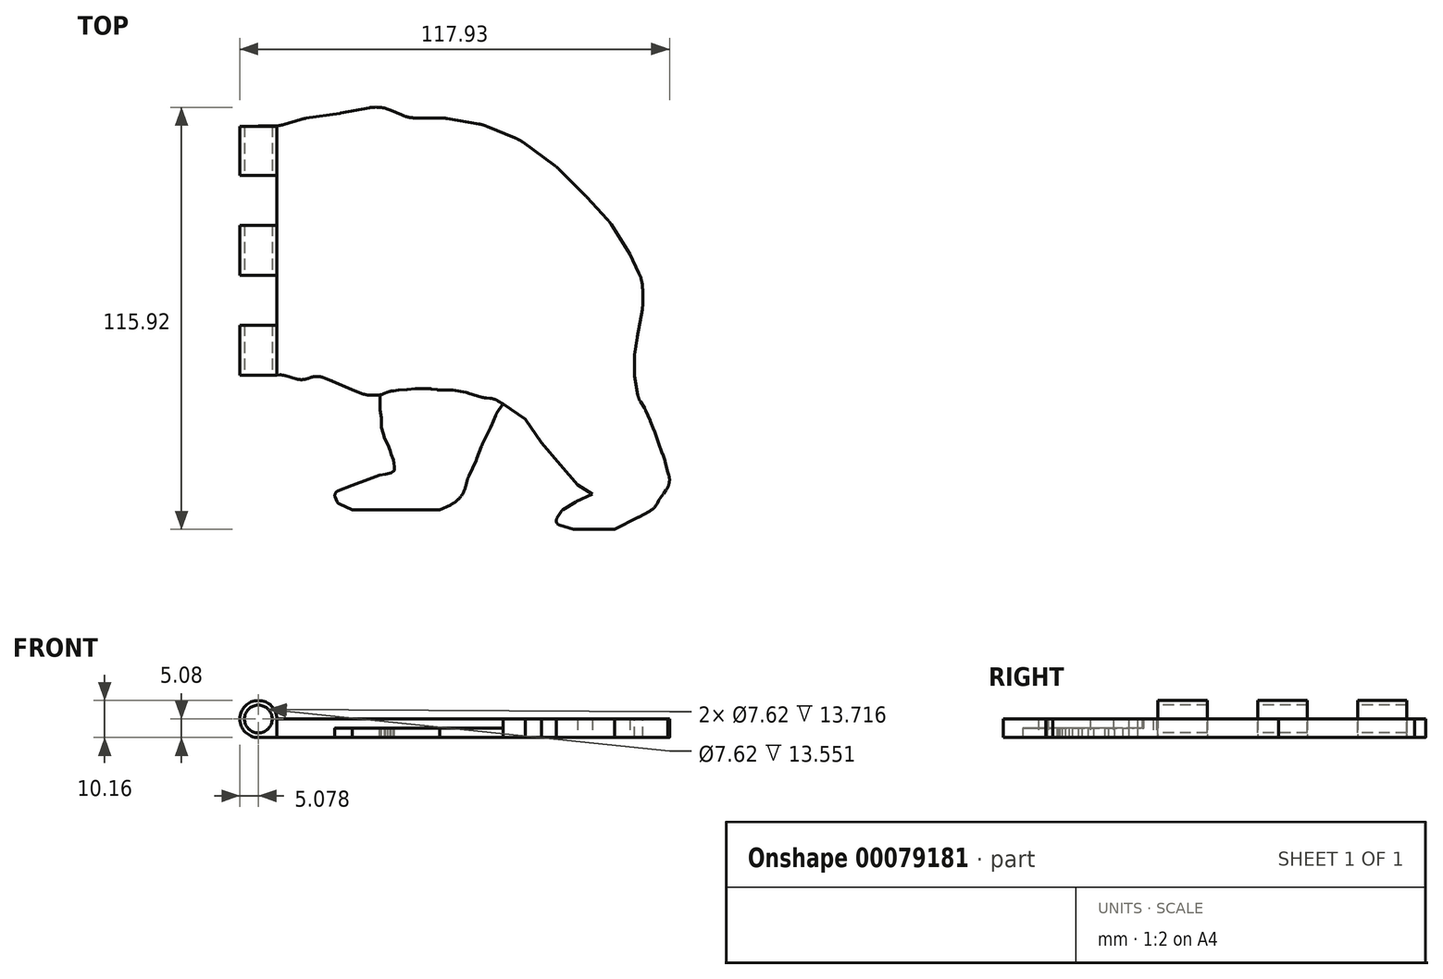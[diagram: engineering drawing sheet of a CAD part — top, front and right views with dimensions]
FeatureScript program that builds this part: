
annotation { "Feature Type Name" : "Feature", "Feature Type Description" : "" }
export const myFeature = defineFeature(function(context is Context, id is Id, definition is map)
    precondition{}
    {
        {
            var Q0;
            Q0=qCreatedBy(makeId("Top.planeOp"),FACE);
            var sketch = newSketch(context, id + "F0", { "sketchPlane" : qUnion([Q0])});
            skLineSegment(sketch, "E0", {"start": v(-108.98, 47.54) * mm, "end": v(-114.56, 51.08) * mm});
            skLineSegment(sketch, "E1", {"start": v(-114.56, 51.08) * mm, "end": v(-115.99, 48.82) * mm});
            skLineSegment(sketch, "E2", {"start": v(-115.99, 48.82) * mm, "end": v(-117.54, 46.98) * mm});
            skLineSegment(sketch, "E3", {"start": v(-117.54, 46.98) * mm, "end": v(-115.49, 40.84) * mm});
            skLineSegment(sketch, "E4", {"start": v(-115.49, 40.84) * mm, "end": v(-119.38, 33.2) * mm});
            skLineSegment(sketch, "E5", {"start": v(-119.38, 33.2) * mm, "end": v(-119.38, 25.58) * mm});
            skLineSegment(sketch, "E6", {"start": v(-119.38, 25.58) * mm, "end": v(-119.38, 18.5) * mm});
            skLineSegment(sketch, "E7", {"start": v(-119.38, 18.5) * mm, "end": v(-122.93, 10.13) * mm});
            skLineSegment(sketch, "E8", {"start": v(-122.93, 10.13) * mm, "end": v(-125.17, 4.36) * mm});
            skLineSegment(sketch, "E9", {"start": v(-125.17, 4.36) * mm, "end": v(-125.17, 0) * mm});
            skLineSegment(sketch, "E10", {"start": v(-125.17, 0) * mm, "end": v(-117.16, -4.2) * mm});
            skLineSegment(sketch, "E11", {"start": v(-117.16, -4.2) * mm, "end": v(-112.7, -1.4) * mm});
            skLineSegment(sketch, "E12", {"start": v(-112.7, -1.4) * mm, "end": v(-103.77, 3.25) * mm});
            skLineSegment(sketch, "E13", {"start": v(-103.77, 3.25) * mm, "end": v(-97.07, 5.48) * mm});
            skLineSegment(sketch, "E14", {"start": v(-97.07, 5.48) * mm, "end": v(-88.5, 7.16) * mm});
            skLineSegment(sketch, "E15", {"start": v(-88.5, 7.16) * mm, "end": v(-93.16, 2.13) * mm});
            skLineSegment(sketch, "E16", {"start": v(-93.16, 2.13) * mm, "end": v(-99.49, -4.94) * mm});
            skLineSegment(sketch, "E17", {"start": v(-99.49, -4.94) * mm, "end": v(-104.32, -11.08) * mm});
            skLineSegment(sketch, "E18", {"start": v(-104.32, -11.08) * mm, "end": v(-106, -14.62) * mm});
            skLineSegment(sketch, "E19", {"start": v(-106, -14.62) * mm, "end": v(-107.86, -19.08) * mm});
            skLineSegment(sketch, "E20", {"start": v(-107.86, -19.08) * mm, "end": v(-110.1, -25.23) * mm});
            skLineSegment(sketch, "E21", {"start": v(-110.1, -25.23) * mm, "end": v(-110.1, -28.95) * mm});
            skLineSegment(sketch, "E22", {"start": v(-110.1, -28.95) * mm, "end": v(-111.77, -33.04) * mm});
            skLineSegment(sketch, "E23", {"start": v(-111.77, -33.04) * mm, "end": v(-109.14, -34.12) * mm});
            skLineSegment(sketch, "E24", {"start": v(-109.14, -34.12) * mm, "end": v(-103.2, -30.8) * mm});
            skLineSegment(sketch, "E25", {"start": v(-103.2, -30.8) * mm, "end": v(-100.6, -27.64) * mm});
            skLineSegment(sketch, "E26", {"start": v(-100.6, -27.64) * mm, "end": v(-97.07, -19.27) * mm});
            skLineSegment(sketch, "E27", {"start": v(-97.07, -19.27) * mm, "end": v(-92.23, -17.4) * mm});
            skLineSegment(sketch, "E28", {"start": v(-92.23, -17.4) * mm, "end": v(-75.66, -17.4) * mm});
            skLineSegment(sketch, "E29", {"start": v(-75.66, -17.4) * mm, "end": v(-63, -11.45) * mm});
            skLineSegment(sketch, "E30", {"start": v(-63, -11.45) * mm, "end": v(-65.24, -20.39) * mm});
            skLineSegment(sketch, "E31", {"start": v(-65.24, -20.39) * mm, "end": v(-67.3, -29.13) * mm});
            skLineSegment(sketch, "E32", {"start": v(-67.3, -29.13) * mm, "end": v(-70.64, -34.9) * mm});
            skLineSegment(sketch, "E33", {"start": v(-70.64, -34.9) * mm, "end": v(-73.06, -36.76) * mm});
            skLineSegment(sketch, "E34", {"start": v(-73.06, -36.76) * mm, "end": v(-80.5, -36.76) * mm});
            skLineSegment(sketch, "E35", {"start": v(-80.5, -36.76) * mm, "end": v(-84.78, -38.62) * mm});
            skLineSegment(sketch, "E36", {"start": v(-84.78, -38.62) * mm, "end": v(-87.95, -42.35) * mm});
            skLineSegment(sketch, "E37", {"start": v(-87.95, -42.35) * mm, "end": v(-90, -44.95) * mm});
            skLineSegment(sketch, "E38", {"start": v(-90, -44.95) * mm, "end": v(-87.38, -47) * mm});
            skLineSegment(sketch, "E39", {"start": v(-87.38, -47) * mm, "end": v(-77.71, -47) * mm});
            skLineSegment(sketch, "E40", {"start": v(-77.71, -47) * mm, "end": v(-69.9, -47) * mm});
            skLineSegment(sketch, "E41", {"start": v(-69.9, -47) * mm, "end": v(-63.38, -45.32) * mm});
            skLineSegment(sketch, "E42", {"start": v(-63.38, -45.32) * mm, "end": v(-55.57, -41.79) * mm});
            skLineSegment(sketch, "E43", {"start": v(-55.57, -41.79) * mm, "end": v(-47.94, -37.7) * mm});
            skLineSegment(sketch, "E44", {"start": v(-47.94, -37.7) * mm, "end": v(-42.73, -32.67) * mm});
            skLineSegment(sketch, "E45", {"start": v(-42.73, -32.67) * mm, "end": v(-40.12, -28.76) * mm});
            skLineSegment(sketch, "E46", {"start": v(-40.12, -28.76) * mm, "end": v(-36.96, -22.62) * mm});
            skLineSegment(sketch, "E47", {"start": v(-36.96, -22.62) * mm, "end": v(-33.8, -16.48) * mm});
            skLineSegment(sketch, "E48", {"start": v(-33.8, -16.48) * mm, "end": v(-29.14, -10.9) * mm});
            skLineSegment(sketch, "E49", {"start": v(-29.14, -10.9) * mm, "end": v(-23.56, -9.03) * mm});
            skLineSegment(sketch, "E50", {"start": v(-23.56, -9.03) * mm, "end": v(-19.1, -8.85) * mm});
            skLineSegment(sketch, "E51", {"start": v(-19.1, -8.85) * mm, "end": v(-13.5, -10.52) * mm});
            skLineSegment(sketch, "E52", {"start": v(-13.5, -10.52) * mm, "end": v(-9.97, -8.85) * mm});
            skLineSegment(sketch, "E53", {"start": v(-9.97, -8.85) * mm, "end": v(-5.5, -10.52) * mm});
            skLineSegment(sketch, "E54", {"start": v(-5.5, -10.52) * mm, "end": v(0, -12.94) * mm});
            skLineSegment(sketch, "E55", {"start": v(0, -12.94) * mm, "end": v(3.99, -14.43) * mm});
            skLineSegment(sketch, "E56", {"start": v(3.99, -14.43) * mm, "end": v(7.7, -14.43) * mm});
            skLineSegment(sketch, "E57", {"start": v(7.7, -14.43) * mm, "end": v(7.7, -18.53) * mm});
            skLineSegment(sketch, "E58", {"start": v(7.7, -18.53) * mm, "end": v(5.29, -22.43) * mm});
            skLineSegment(sketch, "E59", {"start": v(5.29, -22.43) * mm, "end": v(6.22, -25.23) * mm});
            skLineSegment(sketch, "E60", {"start": v(6.22, -25.23) * mm, "end": v(6.96, -29.88) * mm});
            skLineSegment(sketch, "E61", {"start": v(6.96, -29.88) * mm, "end": v(8.45, -33.23) * mm});
            skLineSegment(sketch, "E62", {"start": v(8.45, -33.23) * mm, "end": v(10.5, -35.27) * mm});
            skLineSegment(sketch, "E63", {"start": v(10.5, -35.27) * mm, "end": v(4.54, -37.5) * mm});
            skLineSegment(sketch, "E64", {"start": v(4.54, -37.5) * mm, "end": v(0, -39.18) * mm});
            skLineSegment(sketch, "E65", {"start": v(0, -39.18) * mm, "end": v(-5.13, -41.23) * mm});
            skLineSegment(sketch, "E66", {"start": v(-5.13, -41.23) * mm, "end": v(-4, -44.09) * mm});
            skLineSegment(sketch, "E67", {"start": v(-4, -44.09) * mm, "end": v(0, -45.88) * mm});
            skLineSegment(sketch, "E68", {"start": v(0, -45.88) * mm, "end": v(6.22, -45.88) * mm});
            skLineSegment(sketch, "E69", {"start": v(6.22, -45.88) * mm, "end": v(16.08, -45.88) * mm});
            skLineSegment(sketch, "E70", {"start": v(16.08, -45.88) * mm, "end": v(24.08, -45.88) * mm});
            skLineSegment(sketch, "E71", {"start": v(24.08, -45.88) * mm, "end": v(28.18, -44.02) * mm});
            skLineSegment(sketch, "E72", {"start": v(28.18, -44.02) * mm, "end": v(30.6, -41.6) * mm});
            skLineSegment(sketch, "E73", {"start": v(30.6, -41.6) * mm, "end": v(31.71, -37.32) * mm});
            skLineSegment(sketch, "E74", {"start": v(31.71, -37.32) * mm, "end": v(34.13, -32.11) * mm});
            skLineSegment(sketch, "E75", {"start": v(34.13, -32.11) * mm, "end": v(35.62, -28.2) * mm});
            skLineSegment(sketch, "E76", {"start": v(35.62, -28.2) * mm, "end": v(38.04, -23.18) * mm});
            skLineSegment(sketch, "E77", {"start": v(38.04, -23.18) * mm, "end": v(39.72, -19.27) * mm});
            skLineSegment(sketch, "E78", {"start": v(39.72, -19.27) * mm, "end": v(41.4, -16.85) * mm});
            skLineSegment(sketch, "E79", {"start": v(41.4, -16.85) * mm, "end": v(47.47, -21.06) * mm});
            skLineSegment(sketch, "E80", {"start": v(47.47, -21.06) * mm, "end": v(52, -27.46) * mm});
            skLineSegment(sketch, "E81", {"start": v(52, -27.46) * mm, "end": v(57.2, -33.6) * mm});
            skLineSegment(sketch, "E82", {"start": v(57.2, -33.6) * mm, "end": v(61.86, -39) * mm});
            skLineSegment(sketch, "E83", {"start": v(61.86, -39) * mm, "end": v(65.96, -41.6) * mm});
            skLineSegment(sketch, "E84", {"start": v(65.96, -41.6) * mm, "end": v(61.49, -43.65) * mm});
            skLineSegment(sketch, "E85", {"start": v(61.49, -43.65) * mm, "end": v(57.58, -46.07) * mm});
            skLineSegment(sketch, "E86", {"start": v(57.58, -46.07) * mm, "end": v(55.35, -49.68) * mm});
            skLineSegment(sketch, "E87", {"start": v(55.35, -49.68) * mm, "end": v(57.58, -46.07) * mm});
            skLineSegment(sketch, "E88", {"start": v(55.35, -49.68) * mm, "end": v(60.93, -51.28) * mm});
            skLineSegment(sketch, "E89", {"start": v(60.93, -51.28) * mm, "end": v(68, -51.28) * mm});
            skLineSegment(sketch, "E90", {"start": v(68, -51.28) * mm, "end": v(72.1, -51.28) * mm});
            skLineSegment(sketch, "E91", {"start": v(72.1, -51.28) * mm, "end": v(78.61, -47.93) * mm});
            skLineSegment(sketch, "E92", {"start": v(78.61, -47.93) * mm, "end": v(83.08, -45.5) * mm});
            skLineSegment(sketch, "E93", {"start": v(83.08, -45.5) * mm, "end": v(87.17, -40.49) * mm});
            skLineSegment(sketch, "E94", {"start": v(87.17, -40.49) * mm, "end": v(89.03, -35.09) * mm});
            skLineSegment(sketch, "E95", {"start": v(89.03, -35.09) * mm, "end": v(86.24, -28.95) * mm});
            skLineSegment(sketch, "E96", {"start": v(86.24, -28.95) * mm, "end": v(84.38, -22.06) * mm});
            skLineSegment(sketch, "E97", {"start": v(84.38, -22.06) * mm, "end": v(81.22, -16.85) * mm});
            skLineSegment(sketch, "E98", {"start": v(81.22, -16.85) * mm, "end": v(79.73, -14.25) * mm});
            skLineSegment(sketch, "E99", {"start": v(79.73, -14.25) * mm, "end": v(79.73, -6.99) * mm});
            skLineSegment(sketch, "E100", {"start": v(79.73, -6.99) * mm, "end": v(79.73, 1.76) * mm});
            skLineSegment(sketch, "E101", {"start": v(79.73, 1.76) * mm, "end": v(79.73, 8.64) * mm});
            skLineSegment(sketch, "E102", {"start": v(79.73, 8.64) * mm, "end": v(79.73, 17.02) * mm});
            skLineSegment(sketch, "E103", {"start": v(79.73, 17.02) * mm, "end": v(76.2, 24.28) * mm});
            skLineSegment(sketch, "E104", {"start": v(76.2, 24.28) * mm, "end": v(70.6, 33.2) * mm});
            skLineSegment(sketch, "E105", {"start": v(70.6, 33.2) * mm, "end": v(64.28, 40.1) * mm});
            skLineSegment(sketch, "E106", {"start": v(64.28, 40.1) * mm, "end": v(56.28, 48.1) * mm});
            skLineSegment(sketch, "E107", {"start": v(56.28, 48.1) * mm, "end": v(45.86, 55.73) * mm});
            skLineSegment(sketch, "E108", {"start": v(45.86, 55.73) * mm, "end": v(36, 59.82) * mm});
            skLineSegment(sketch, "E109", {"start": v(36, 59.82) * mm, "end": v(25.2, 61.68) * mm});
            skLineSegment(sketch, "E110", {"start": v(25.2, 61.68) * mm, "end": v(15.52, 61.68) * mm});
            skLineSegment(sketch, "E111", {"start": v(15.52, 61.68) * mm, "end": v(7.7, 65.03) * mm});
            skLineSegment(sketch, "E112", {"start": v(7.7, 65.03) * mm, "end": v(-3.27, 62.99) * mm});
            skLineSegment(sketch, "E113", {"start": v(-3.27, 62.99) * mm, "end": v(-13.32, 61.5) * mm});
            skLineSegment(sketch, "E114", {"start": v(-13.32, 61.5) * mm, "end": v(-20.2, 59.45) * mm});
            skLineSegment(sketch, "E115", {"start": v(-20.2, 59.45) * mm, "end": v(-26.35, 59.45) * mm});
            skLineSegment(sketch, "E116", {"start": v(-26.35, 59.45) * mm, "end": v(-32.68, 61.68) * mm});
            skLineSegment(sketch, "E117", {"start": v(-32.68, 61.68) * mm, "end": v(-42.17, 64.47) * mm});
            skLineSegment(sketch, "E118", {"start": v(-42.17, 64.47) * mm, "end": v(-50.36, 64.47) * mm});
            skLineSegment(sketch, "E119", {"start": v(-50.36, 64.47) * mm, "end": v(-59.1, 59.08) * mm});
            skLineSegment(sketch, "E120", {"start": v(-59.1, 59.08) * mm, "end": v(-66.55, 53.87) * mm});
            skLineSegment(sketch, "E121", {"start": v(-66.55, 53.87) * mm, "end": v(-76.6, 50.14) * mm});
            skLineSegment(sketch, "E122", {"start": v(-76.6, 50.14) * mm, "end": v(-85.9, 48.47) * mm});
            skLineSegment(sketch, "E123", {"start": v(-85.9, 48.47) * mm, "end": v(-95.02, 46.6) * mm});
            skLineSegment(sketch, "E124", {"start": v(-95.02, 46.6) * mm, "end": v(-101.53, 46.05) * mm});
            skLineSegment(sketch, "E125", {"start": v(-101.53, 46.05) * mm, "end": v(-108.98, 47.54) * mm});
            skSolve(sketch);
        }
        {
            var Q0;
            Q0=qSketchRegion(id+"F0",true);
            extrude(context, id + "F1", {"entities" : qUnion([Q0]), "depth" : 5.08 * mm});
        }
        {
            var Q0;
            Q0=makeQuery(id+"F1.opExtrude","SWEPT_EDGE",EDGE,{"disambiguationData":[OSD([sQuery(id+"F0.wireOp",EDGE,"E117"),sQuery(id+"F0.wireOp",EDGE,"E118")])]});
            var Q1;
            Q1=makeQuery(id+"F1.opExtrude","SWEPT_EDGE",EDGE,{"disambiguationData":[OSD([sQuery(id+"F0.wireOp",EDGE,"E118"),sQuery(id+"F0.wireOp",EDGE,"E119")])]});
            var Q2;
            Q2=makeQuery(id+"F1.opExtrude","SWEPT_EDGE",EDGE,{"disambiguationData":[OSD([sQuery(id+"F0.wireOp",EDGE,"E119"),sQuery(id+"F0.wireOp",EDGE,"E120")])]});
            var Q3;
            Q3=makeQuery(id+"F1.opExtrude","SWEPT_EDGE",EDGE,{"disambiguationData":[OSD([sQuery(id+"F0.wireOp",EDGE,"E120"),sQuery(id+"F0.wireOp",EDGE,"E121")])]});
            var Q4;
            Q4=makeQuery(id+"F1.opExtrude","SWEPT_EDGE",EDGE,{"disambiguationData":[OSD([sQuery(id+"F0.wireOp",EDGE,"E121"),sQuery(id+"F0.wireOp",EDGE,"E122")])]});
            var Q5;
            Q5=makeQuery(id+"F1.opExtrude","SWEPT_EDGE",EDGE,{"disambiguationData":[OSD([sQuery(id+"F0.wireOp",EDGE,"E116"),sQuery(id+"F0.wireOp",EDGE,"E117")])]});
            var Q6;
            Q6=makeQuery(id+"F1.opExtrude","SWEPT_EDGE",EDGE,{"disambiguationData":[OSD([sQuery(id+"F0.wireOp",EDGE,"E115"),sQuery(id+"F0.wireOp",EDGE,"E116")])]});
            var Q7;
            Q7=makeQuery(id+"F1.opExtrude","SWEPT_EDGE",EDGE,{"disambiguationData":[OSD([sQuery(id+"F0.wireOp",EDGE,"E114"),sQuery(id+"F0.wireOp",EDGE,"E115")])]});
            var Q8;
            Q8=makeQuery(id+"F1.opExtrude","SWEPT_EDGE",EDGE,{"disambiguationData":[OSD([sQuery(id+"F0.wireOp",EDGE,"E113"),sQuery(id+"F0.wireOp",EDGE,"E114")])]});
            var Q9;
            Q9=makeQuery(id+"F1.opExtrude","SWEPT_EDGE",EDGE,{"disambiguationData":[OSD([sQuery(id+"F0.wireOp",EDGE,"E112"),sQuery(id+"F0.wireOp",EDGE,"E113")])]});
            var Q10;
            Q10=makeQuery(id+"F1.opExtrude","SWEPT_EDGE",EDGE,{"disambiguationData":[OSD([sQuery(id+"F0.wireOp",EDGE,"E111"),sQuery(id+"F0.wireOp",EDGE,"E112")])]});
            var Q11;
            Q11=makeQuery(id+"F1.opExtrude","SWEPT_EDGE",EDGE,{"disambiguationData":[OSD([sQuery(id+"F0.wireOp",EDGE,"E110"),sQuery(id+"F0.wireOp",EDGE,"E111")])]});
            var Q12;
            Q12=makeQuery(id+"F1.opExtrude","SWEPT_EDGE",EDGE,{"disambiguationData":[OSD([sQuery(id+"F0.wireOp",EDGE,"E109"),sQuery(id+"F0.wireOp",EDGE,"E110")])]});
            var Q13;
            Q13=makeQuery(id+"F1.opExtrude","SWEPT_EDGE",EDGE,{"disambiguationData":[OSD([sQuery(id+"F0.wireOp",EDGE,"E107"),sQuery(id+"F0.wireOp",EDGE,"E108")])]});
            var Q14;
            Q14=makeQuery(id+"F1.opExtrude","SWEPT_EDGE",EDGE,{"disambiguationData":[OSD([sQuery(id+"F0.wireOp",EDGE,"E108"),sQuery(id+"F0.wireOp",EDGE,"E109")])]});
            var Q15;
            Q15=makeQuery(id+"F1.opExtrude","SWEPT_EDGE",EDGE,{"disambiguationData":[OSD([sQuery(id+"F0.wireOp",EDGE,"E106"),sQuery(id+"F0.wireOp",EDGE,"E107")])]});
            var Q16;
            Q16=makeQuery(id+"F1.opExtrude","SWEPT_EDGE",EDGE,{"disambiguationData":[OSD([sQuery(id+"F0.wireOp",EDGE,"E102"),sQuery(id+"F0.wireOp",EDGE,"E103")])]});
            var Q17;
            Q17=makeQuery(id+"F1.opExtrude","SWEPT_EDGE",EDGE,{"disambiguationData":[OSD([sQuery(id+"F0.wireOp",EDGE,"E104"),sQuery(id+"F0.wireOp",EDGE,"E105")])]});
            var Q18;
            Q18=makeQuery(id+"F1.opExtrude","SWEPT_EDGE",EDGE,{"disambiguationData":[OSD([sQuery(id+"F0.wireOp",EDGE,"E105"),sQuery(id+"F0.wireOp",EDGE,"E106")])]});
            fillet(context, id + "F2", {"entities" : qUnion([Q0, Q1, Q2, Q3, Q4, Q5, Q6, Q7, Q8, Q9, Q10, Q11, Q12, Q13, Q14, Q15, Q16, Q17, Q18]), "radius" : 10.16 * mm, "tangentPropagation" : true, "allowEdgeOverflow" : false});
        }
        {
            var Q0;
            Q0=makeQuery(id+"F1.opExtrude","CAP_FACE",FACE,{"disambiguationData":[OSD([sQuery(id+"F0.wireOp",EDGE,"E0"),sQuery(id+"F0.wireOp",EDGE,"E1"),sQuery(id+"F0.wireOp",EDGE,"E2"),sQuery(id+"F0.wireOp",EDGE,"E3"),sQuery(id+"F0.wireOp",EDGE,"E4"),sQuery(id+"F0.wireOp",EDGE,"E5"),sQuery(id+"F0.wireOp",EDGE,"E6"),sQuery(id+"F0.wireOp",EDGE,"E7"),sQuery(id+"F0.wireOp",EDGE,"E8"),sQuery(id+"F0.wireOp",EDGE,"E9"),sQuery(id+"F0.wireOp",EDGE,"E10"),sQuery(id+"F0.wireOp",EDGE,"E11"),sQuery(id+"F0.wireOp",EDGE,"E12"),sQuery(id+"F0.wireOp",EDGE,"E13"),sQuery(id+"F0.wireOp",EDGE,"E14"),sQuery(id+"F0.wireOp",EDGE,"E15"),sQuery(id+"F0.wireOp",EDGE,"E16"),sQuery(id+"F0.wireOp",EDGE,"E17"),sQuery(id+"F0.wireOp",EDGE,"E18"),sQuery(id+"F0.wireOp",EDGE,"E19"),sQuery(id+"F0.wireOp",EDGE,"E20"),sQuery(id+"F0.wireOp",EDGE,"E21"),sQuery(id+"F0.wireOp",EDGE,"E22"),sQuery(id+"F0.wireOp",EDGE,"E23"),sQuery(id+"F0.wireOp",EDGE,"E24"),sQuery(id+"F0.wireOp",EDGE,"E25"),sQuery(id+"F0.wireOp",EDGE,"E26"),sQuery(id+"F0.wireOp",EDGE,"E27"),sQuery(id+"F0.wireOp",EDGE,"E28"),sQuery(id+"F0.wireOp",EDGE,"E29"),sQuery(id+"F0.wireOp",EDGE,"E30"),sQuery(id+"F0.wireOp",EDGE,"E31"),sQuery(id+"F0.wireOp",EDGE,"E32"),sQuery(id+"F0.wireOp",EDGE,"E33"),sQuery(id+"F0.wireOp",EDGE,"E34"),sQuery(id+"F0.wireOp",EDGE,"E35"),sQuery(id+"F0.wireOp",EDGE,"E36"),sQuery(id+"F0.wireOp",EDGE,"E37"),sQuery(id+"F0.wireOp",EDGE,"E38"),sQuery(id+"F0.wireOp",EDGE,"E39"),sQuery(id+"F0.wireOp",EDGE,"E40"),sQuery(id+"F0.wireOp",EDGE,"E41"),sQuery(id+"F0.wireOp",EDGE,"E42"),sQuery(id+"F0.wireOp",EDGE,"E43"),sQuery(id+"F0.wireOp",EDGE,"E44"),sQuery(id+"F0.wireOp",EDGE,"E45"),sQuery(id+"F0.wireOp",EDGE,"E46"),sQuery(id+"F0.wireOp",EDGE,"E47"),sQuery(id+"F0.wireOp",EDGE,"E48"),sQuery(id+"F0.wireOp",EDGE,"E49"),sQuery(id+"F0.wireOp",EDGE,"E50"),sQuery(id+"F0.wireOp",EDGE,"E51"),sQuery(id+"F0.wireOp",EDGE,"E52"),sQuery(id+"F0.wireOp",EDGE,"E53"),sQuery(id+"F0.wireOp",EDGE,"E54"),sQuery(id+"F0.wireOp",EDGE,"E55"),sQuery(id+"F0.wireOp",EDGE,"E56"),sQuery(id+"F0.wireOp",EDGE,"E57"),sQuery(id+"F0.wireOp",EDGE,"E58"),sQuery(id+"F0.wireOp",EDGE,"E59"),sQuery(id+"F0.wireOp",EDGE,"E60"),sQuery(id+"F0.wireOp",EDGE,"E61"),sQuery(id+"F0.wireOp",EDGE,"E62"),sQuery(id+"F0.wireOp",EDGE,"E63"),sQuery(id+"F0.wireOp",EDGE,"E64"),sQuery(id+"F0.wireOp",EDGE,"E65"),sQuery(id+"F0.wireOp",EDGE,"E66"),sQuery(id+"F0.wireOp",EDGE,"E67"),sQuery(id+"F0.wireOp",EDGE,"E68"),sQuery(id+"F0.wireOp",EDGE,"E69"),sQuery(id+"F0.wireOp",EDGE,"E70"),sQuery(id+"F0.wireOp",EDGE,"E71"),sQuery(id+"F0.wireOp",EDGE,"E72"),sQuery(id+"F0.wireOp",EDGE,"E73"),sQuery(id+"F0.wireOp",EDGE,"E74"),sQuery(id+"F0.wireOp",EDGE,"E75"),sQuery(id+"F0.wireOp",EDGE,"E76"),sQuery(id+"F0.wireOp",EDGE,"E77"),sQuery(id+"F0.wireOp",EDGE,"E78"),sQuery(id+"F0.wireOp",EDGE,"E79"),sQuery(id+"F0.wireOp",EDGE,"E80"),sQuery(id+"F0.wireOp",EDGE,"E81"),sQuery(id+"F0.wireOp",EDGE,"E82"),sQuery(id+"F0.wireOp",EDGE,"E83"),sQuery(id+"F0.wireOp",EDGE,"E84"),sQuery(id+"F0.wireOp",EDGE,"E85"),sQuery(id+"F0.wireOp",EDGE,"E87"),sQuery(id+"F0.wireOp",EDGE,"E88"),sQuery(id+"F0.wireOp",EDGE,"E89"),sQuery(id+"F0.wireOp",EDGE,"E90"),sQuery(id+"F0.wireOp",EDGE,"E91"),sQuery(id+"F0.wireOp",EDGE,"E92"),sQuery(id+"F0.wireOp",EDGE,"E93"),sQuery(id+"F0.wireOp",EDGE,"E94"),sQuery(id+"F0.wireOp",EDGE,"E95"),sQuery(id+"F0.wireOp",EDGE,"E96"),sQuery(id+"F0.wireOp",EDGE,"E97"),sQuery(id+"F0.wireOp",EDGE,"E98"),sQuery(id+"F0.wireOp",EDGE,"E99"),sQuery(id+"F0.wireOp",EDGE,"E100"),sQuery(id+"F0.wireOp",EDGE,"E101"),sQuery(id+"F0.wireOp",EDGE,"E102"),sQuery(id+"F0.wireOp",EDGE,"E103"),sQuery(id+"F0.wireOp",EDGE,"E104"),sQuery(id+"F0.wireOp",EDGE,"E105"),sQuery(id+"F0.wireOp",EDGE,"E106"),sQuery(id+"F0.wireOp",EDGE,"E107"),sQuery(id+"F0.wireOp",EDGE,"E108"),sQuery(id+"F0.wireOp",EDGE,"E109"),sQuery(id+"F0.wireOp",EDGE,"E110"),sQuery(id+"F0.wireOp",EDGE,"E111"),sQuery(id+"F0.wireOp",EDGE,"E112"),sQuery(id+"F0.wireOp",EDGE,"E113"),sQuery(id+"F0.wireOp",EDGE,"E114"),sQuery(id+"F0.wireOp",EDGE,"E115"),sQuery(id+"F0.wireOp",EDGE,"E116"),sQuery(id+"F0.wireOp",EDGE,"E117"),sQuery(id+"F0.wireOp",EDGE,"E118"),sQuery(id+"F0.wireOp",EDGE,"E119"),sQuery(id+"F0.wireOp",EDGE,"E120"),sQuery(id+"F0.wireOp",EDGE,"E121"),sQuery(id+"F0.wireOp",EDGE,"E122"),sQuery(id+"F0.wireOp",EDGE,"E123"),sQuery(id+"F0.wireOp",EDGE,"E124"),sQuery(id+"F0.wireOp",EDGE,"E125")])],"isStart":false});
            var sketch = newSketch(context, id + "F3", { "sketchPlane" : qUnion([Q0])});
            skLineSegment(sketch, "E126", {"start": v(79.73, 14.68) * mm, "end": v(79.73, 9.47) * mm});
            skLineSegment(sketch, "E127", {"start": v(79.73, 9.47) * mm, "end": v(78.29, 1.47) * mm});
            skLineSegment(sketch, "E128", {"start": v(78.29, 1.47) * mm, "end": v(77.45, -3.82) * mm});
            skLineSegment(sketch, "E129", {"start": v(77.45, -3.82) * mm, "end": v(77.45, -8.77) * mm});
            skLineSegment(sketch, "E130", {"start": v(77.45, -8.77) * mm, "end": v(79.94, -14.62) * mm});
            skLineSegment(sketch, "E131", {"start": v(79.94, -14.62) * mm, "end": v(89.3, -16.02) * mm});
            skLineSegment(sketch, "E132", {"start": v(89.3, -16.02) * mm, "end": v(87.14, 16.67) * mm});
            skLineSegment(sketch, "E133", {"start": v(87.14, 16.67) * mm, "end": v(79.73, 14.68) * mm});
            skSolve(sketch);
        }
        {
            var Q0;
            Q0=qSketchRegion(id+"F3",true);
            extrude(context, id + "F4", {"entities" : qUnion([Q0]), "operationType" : NewBodyOperationType.REMOVE, "oppositeDirection" : true, "depth" : 25.4 * mm});
        }
        {
            var Q0;
            Q0=makeQuery(id+"F1.opExtrude","CAP_FACE",FACE,{"disambiguationData":[OSD([sQuery(id+"F0.wireOp",EDGE,"E0"),sQuery(id+"F0.wireOp",EDGE,"E1"),sQuery(id+"F0.wireOp",EDGE,"E2"),sQuery(id+"F0.wireOp",EDGE,"E3"),sQuery(id+"F0.wireOp",EDGE,"E4"),sQuery(id+"F0.wireOp",EDGE,"E5"),sQuery(id+"F0.wireOp",EDGE,"E6"),sQuery(id+"F0.wireOp",EDGE,"E7"),sQuery(id+"F0.wireOp",EDGE,"E8"),sQuery(id+"F0.wireOp",EDGE,"E9"),sQuery(id+"F0.wireOp",EDGE,"E10"),sQuery(id+"F0.wireOp",EDGE,"E11"),sQuery(id+"F0.wireOp",EDGE,"E12"),sQuery(id+"F0.wireOp",EDGE,"E13"),sQuery(id+"F0.wireOp",EDGE,"E14"),sQuery(id+"F0.wireOp",EDGE,"E15"),sQuery(id+"F0.wireOp",EDGE,"E16"),sQuery(id+"F0.wireOp",EDGE,"E17"),sQuery(id+"F0.wireOp",EDGE,"E18"),sQuery(id+"F0.wireOp",EDGE,"E19"),sQuery(id+"F0.wireOp",EDGE,"E20"),sQuery(id+"F0.wireOp",EDGE,"E21"),sQuery(id+"F0.wireOp",EDGE,"E22"),sQuery(id+"F0.wireOp",EDGE,"E23"),sQuery(id+"F0.wireOp",EDGE,"E24"),sQuery(id+"F0.wireOp",EDGE,"E25"),sQuery(id+"F0.wireOp",EDGE,"E26"),sQuery(id+"F0.wireOp",EDGE,"E27"),sQuery(id+"F0.wireOp",EDGE,"E28"),sQuery(id+"F0.wireOp",EDGE,"E29"),sQuery(id+"F0.wireOp",EDGE,"E30"),sQuery(id+"F0.wireOp",EDGE,"E31"),sQuery(id+"F0.wireOp",EDGE,"E32"),sQuery(id+"F0.wireOp",EDGE,"E33"),sQuery(id+"F0.wireOp",EDGE,"E34"),sQuery(id+"F0.wireOp",EDGE,"E35"),sQuery(id+"F0.wireOp",EDGE,"E36"),sQuery(id+"F0.wireOp",EDGE,"E37"),sQuery(id+"F0.wireOp",EDGE,"E38"),sQuery(id+"F0.wireOp",EDGE,"E39"),sQuery(id+"F0.wireOp",EDGE,"E40"),sQuery(id+"F0.wireOp",EDGE,"E41"),sQuery(id+"F0.wireOp",EDGE,"E42"),sQuery(id+"F0.wireOp",EDGE,"E43"),sQuery(id+"F0.wireOp",EDGE,"E44"),sQuery(id+"F0.wireOp",EDGE,"E45"),sQuery(id+"F0.wireOp",EDGE,"E46"),sQuery(id+"F0.wireOp",EDGE,"E47"),sQuery(id+"F0.wireOp",EDGE,"E48"),sQuery(id+"F0.wireOp",EDGE,"E49"),sQuery(id+"F0.wireOp",EDGE,"E50"),sQuery(id+"F0.wireOp",EDGE,"E51"),sQuery(id+"F0.wireOp",EDGE,"E52"),sQuery(id+"F0.wireOp",EDGE,"E53"),sQuery(id+"F0.wireOp",EDGE,"E54"),sQuery(id+"F0.wireOp",EDGE,"E55"),sQuery(id+"F0.wireOp",EDGE,"E56"),sQuery(id+"F0.wireOp",EDGE,"E57"),sQuery(id+"F0.wireOp",EDGE,"E58"),sQuery(id+"F0.wireOp",EDGE,"E59"),sQuery(id+"F0.wireOp",EDGE,"E60"),sQuery(id+"F0.wireOp",EDGE,"E61"),sQuery(id+"F0.wireOp",EDGE,"E62"),sQuery(id+"F0.wireOp",EDGE,"E63"),sQuery(id+"F0.wireOp",EDGE,"E64"),sQuery(id+"F0.wireOp",EDGE,"E65"),sQuery(id+"F0.wireOp",EDGE,"E66"),sQuery(id+"F0.wireOp",EDGE,"E67"),sQuery(id+"F0.wireOp",EDGE,"E68"),sQuery(id+"F0.wireOp",EDGE,"E69"),sQuery(id+"F0.wireOp",EDGE,"E70"),sQuery(id+"F0.wireOp",EDGE,"E71"),sQuery(id+"F0.wireOp",EDGE,"E72"),sQuery(id+"F0.wireOp",EDGE,"E73"),sQuery(id+"F0.wireOp",EDGE,"E74"),sQuery(id+"F0.wireOp",EDGE,"E75"),sQuery(id+"F0.wireOp",EDGE,"E76"),sQuery(id+"F0.wireOp",EDGE,"E77"),sQuery(id+"F0.wireOp",EDGE,"E78"),sQuery(id+"F0.wireOp",EDGE,"E79"),sQuery(id+"F0.wireOp",EDGE,"E80"),sQuery(id+"F0.wireOp",EDGE,"E81"),sQuery(id+"F0.wireOp",EDGE,"E82"),sQuery(id+"F0.wireOp",EDGE,"E83"),sQuery(id+"F0.wireOp",EDGE,"E84"),sQuery(id+"F0.wireOp",EDGE,"E85"),sQuery(id+"F0.wireOp",EDGE,"E87"),sQuery(id+"F0.wireOp",EDGE,"E88"),sQuery(id+"F0.wireOp",EDGE,"E89"),sQuery(id+"F0.wireOp",EDGE,"E90"),sQuery(id+"F0.wireOp",EDGE,"E91"),sQuery(id+"F0.wireOp",EDGE,"E92"),sQuery(id+"F0.wireOp",EDGE,"E93"),sQuery(id+"F0.wireOp",EDGE,"E94"),sQuery(id+"F0.wireOp",EDGE,"E95"),sQuery(id+"F0.wireOp",EDGE,"E96"),sQuery(id+"F0.wireOp",EDGE,"E97"),sQuery(id+"F0.wireOp",EDGE,"E98"),sQuery(id+"F0.wireOp",EDGE,"E99"),sQuery(id+"F0.wireOp",EDGE,"E100"),sQuery(id+"F0.wireOp",EDGE,"E101"),sQuery(id+"F0.wireOp",EDGE,"E102"),sQuery(id+"F0.wireOp",EDGE,"E103"),sQuery(id+"F0.wireOp",EDGE,"E104"),sQuery(id+"F0.wireOp",EDGE,"E105"),sQuery(id+"F0.wireOp",EDGE,"E106"),sQuery(id+"F0.wireOp",EDGE,"E107"),sQuery(id+"F0.wireOp",EDGE,"E108"),sQuery(id+"F0.wireOp",EDGE,"E109"),sQuery(id+"F0.wireOp",EDGE,"E110"),sQuery(id+"F0.wireOp",EDGE,"E111"),sQuery(id+"F0.wireOp",EDGE,"E112"),sQuery(id+"F0.wireOp",EDGE,"E113"),sQuery(id+"F0.wireOp",EDGE,"E114"),sQuery(id+"F0.wireOp",EDGE,"E115"),sQuery(id+"F0.wireOp",EDGE,"E116"),sQuery(id+"F0.wireOp",EDGE,"E117"),sQuery(id+"F0.wireOp",EDGE,"E118"),sQuery(id+"F0.wireOp",EDGE,"E119"),sQuery(id+"F0.wireOp",EDGE,"E120"),sQuery(id+"F0.wireOp",EDGE,"E121"),sQuery(id+"F0.wireOp",EDGE,"E122"),sQuery(id+"F0.wireOp",EDGE,"E123"),sQuery(id+"F0.wireOp",EDGE,"E124"),sQuery(id+"F0.wireOp",EDGE,"E125")])],"isStart":false});
            var sketch = newSketch(context, id + "F5", { "sketchPlane" : qUnion([Q0])});
            skLineSegment(sketch, "E134", {"start": v(77.45, -8.77) * mm, "end": v(78.59, -15.36) * mm});
            skPoint(sketch, "E134.endSnap0", {"position": v(78.59, -11.45) * mm});
            skLineSegment(sketch, "E135", {"start": v(78.59, -15.36) * mm, "end": v(80.45, -18.31) * mm});
            skLineSegment(sketch, "E136", {"start": v(80.45, -18.31) * mm, "end": v(81.83, -21.47) * mm});
            skLineSegment(sketch, "E137", {"start": v(81.83, -21.47) * mm, "end": v(82.91, -24.13) * mm});
            skLineSegment(sketch, "E138", {"start": v(82.91, -24.13) * mm, "end": v(84, -27.19) * mm});
            skLineSegment(sketch, "E139", {"start": v(84, -27.19) * mm, "end": v(85.18, -30.54) * mm});
            skLineSegment(sketch, "E140", {"start": v(85.18, -30.54) * mm, "end": v(85.87, -32.6) * mm});
            skLineSegment(sketch, "E141", {"start": v(85.87, -32.6) * mm, "end": v(86.56, -35.17) * mm});
            skLineSegment(sketch, "E142", {"start": v(86.56, -35.17) * mm, "end": v(87.12, -37.13) * mm});
            skLineSegment(sketch, "E143", {"start": v(87.12, -37.13) * mm, "end": v(87.12, -38.66) * mm});
            skLineSegment(sketch, "E144", {"start": v(87.12, -38.66) * mm, "end": v(86.49, -40.05) * mm});
            skLineSegment(sketch, "E145", {"start": v(86.49, -40.05) * mm, "end": v(85.44, -41.52) * mm});
            skLineSegment(sketch, "E146", {"start": v(85.44, -41.52) * mm, "end": v(84.33, -42.98) * mm});
            skLineSegment(sketch, "E147", {"start": v(84.33, -42.98) * mm, "end": v(83.08, -45.5) * mm});
            skLineSegment(sketch, "E148", {"start": v(83.08, -45.5) * mm, "end": v(104.68, -48.21) * mm});
            skLineSegment(sketch, "E149", {"start": v(104.68, -48.21) * mm, "end": v(104.82, -10.5) * mm});
            skLineSegment(sketch, "E150", {"start": v(104.82, -10.5) * mm, "end": v(77.45, -8.77) * mm});
            skSolve(sketch);
        }
        {
            var Q0;
            Q0=qSketchRegion(id+"F5",true);
            extrude(context, id + "F6", {"entities" : qUnion([Q0]), "operationType" : NewBodyOperationType.REMOVE, "oppositeDirection" : true, "depth" : 25.4 * mm});
        }
        {
            var Q0;
            Q0=makeQuery(id+"F1.opExtrude","CAP_FACE",FACE,{"disambiguationData":[OSD([sQuery(id+"F0.wireOp",EDGE,"E0"),sQuery(id+"F0.wireOp",EDGE,"E1"),sQuery(id+"F0.wireOp",EDGE,"E2"),sQuery(id+"F0.wireOp",EDGE,"E3"),sQuery(id+"F0.wireOp",EDGE,"E4"),sQuery(id+"F0.wireOp",EDGE,"E5"),sQuery(id+"F0.wireOp",EDGE,"E6"),sQuery(id+"F0.wireOp",EDGE,"E7"),sQuery(id+"F0.wireOp",EDGE,"E8"),sQuery(id+"F0.wireOp",EDGE,"E9"),sQuery(id+"F0.wireOp",EDGE,"E10"),sQuery(id+"F0.wireOp",EDGE,"E11"),sQuery(id+"F0.wireOp",EDGE,"E12"),sQuery(id+"F0.wireOp",EDGE,"E13"),sQuery(id+"F0.wireOp",EDGE,"E14"),sQuery(id+"F0.wireOp",EDGE,"E15"),sQuery(id+"F0.wireOp",EDGE,"E16"),sQuery(id+"F0.wireOp",EDGE,"E17"),sQuery(id+"F0.wireOp",EDGE,"E18"),sQuery(id+"F0.wireOp",EDGE,"E19"),sQuery(id+"F0.wireOp",EDGE,"E20"),sQuery(id+"F0.wireOp",EDGE,"E21"),sQuery(id+"F0.wireOp",EDGE,"E22"),sQuery(id+"F0.wireOp",EDGE,"E23"),sQuery(id+"F0.wireOp",EDGE,"E24"),sQuery(id+"F0.wireOp",EDGE,"E25"),sQuery(id+"F0.wireOp",EDGE,"E26"),sQuery(id+"F0.wireOp",EDGE,"E27"),sQuery(id+"F0.wireOp",EDGE,"E28"),sQuery(id+"F0.wireOp",EDGE,"E29"),sQuery(id+"F0.wireOp",EDGE,"E30"),sQuery(id+"F0.wireOp",EDGE,"E31"),sQuery(id+"F0.wireOp",EDGE,"E32"),sQuery(id+"F0.wireOp",EDGE,"E33"),sQuery(id+"F0.wireOp",EDGE,"E34"),sQuery(id+"F0.wireOp",EDGE,"E35"),sQuery(id+"F0.wireOp",EDGE,"E36"),sQuery(id+"F0.wireOp",EDGE,"E37"),sQuery(id+"F0.wireOp",EDGE,"E38"),sQuery(id+"F0.wireOp",EDGE,"E39"),sQuery(id+"F0.wireOp",EDGE,"E40"),sQuery(id+"F0.wireOp",EDGE,"E41"),sQuery(id+"F0.wireOp",EDGE,"E42"),sQuery(id+"F0.wireOp",EDGE,"E43"),sQuery(id+"F0.wireOp",EDGE,"E44"),sQuery(id+"F0.wireOp",EDGE,"E45"),sQuery(id+"F0.wireOp",EDGE,"E46"),sQuery(id+"F0.wireOp",EDGE,"E47"),sQuery(id+"F0.wireOp",EDGE,"E48"),sQuery(id+"F0.wireOp",EDGE,"E49"),sQuery(id+"F0.wireOp",EDGE,"E50"),sQuery(id+"F0.wireOp",EDGE,"E51"),sQuery(id+"F0.wireOp",EDGE,"E52"),sQuery(id+"F0.wireOp",EDGE,"E53"),sQuery(id+"F0.wireOp",EDGE,"E54"),sQuery(id+"F0.wireOp",EDGE,"E55"),sQuery(id+"F0.wireOp",EDGE,"E56"),sQuery(id+"F0.wireOp",EDGE,"E57"),sQuery(id+"F0.wireOp",EDGE,"E58"),sQuery(id+"F0.wireOp",EDGE,"E59"),sQuery(id+"F0.wireOp",EDGE,"E60"),sQuery(id+"F0.wireOp",EDGE,"E61"),sQuery(id+"F0.wireOp",EDGE,"E62"),sQuery(id+"F0.wireOp",EDGE,"E63"),sQuery(id+"F0.wireOp",EDGE,"E64"),sQuery(id+"F0.wireOp",EDGE,"E65"),sQuery(id+"F0.wireOp",EDGE,"E66"),sQuery(id+"F0.wireOp",EDGE,"E67"),sQuery(id+"F0.wireOp",EDGE,"E68"),sQuery(id+"F0.wireOp",EDGE,"E69"),sQuery(id+"F0.wireOp",EDGE,"E70"),sQuery(id+"F0.wireOp",EDGE,"E71"),sQuery(id+"F0.wireOp",EDGE,"E72"),sQuery(id+"F0.wireOp",EDGE,"E73"),sQuery(id+"F0.wireOp",EDGE,"E74"),sQuery(id+"F0.wireOp",EDGE,"E75"),sQuery(id+"F0.wireOp",EDGE,"E76"),sQuery(id+"F0.wireOp",EDGE,"E77"),sQuery(id+"F0.wireOp",EDGE,"E78"),sQuery(id+"F0.wireOp",EDGE,"E79"),sQuery(id+"F0.wireOp",EDGE,"E80"),sQuery(id+"F0.wireOp",EDGE,"E81"),sQuery(id+"F0.wireOp",EDGE,"E82"),sQuery(id+"F0.wireOp",EDGE,"E83"),sQuery(id+"F0.wireOp",EDGE,"E84"),sQuery(id+"F0.wireOp",EDGE,"E85"),sQuery(id+"F0.wireOp",EDGE,"E87"),sQuery(id+"F0.wireOp",EDGE,"E88"),sQuery(id+"F0.wireOp",EDGE,"E89"),sQuery(id+"F0.wireOp",EDGE,"E90"),sQuery(id+"F0.wireOp",EDGE,"E91"),sQuery(id+"F0.wireOp",EDGE,"E92"),sQuery(id+"F0.wireOp",EDGE,"E93"),sQuery(id+"F0.wireOp",EDGE,"E94"),sQuery(id+"F0.wireOp",EDGE,"E95"),sQuery(id+"F0.wireOp",EDGE,"E96"),sQuery(id+"F0.wireOp",EDGE,"E97"),sQuery(id+"F0.wireOp",EDGE,"E98"),sQuery(id+"F0.wireOp",EDGE,"E99"),sQuery(id+"F0.wireOp",EDGE,"E100"),sQuery(id+"F0.wireOp",EDGE,"E101"),sQuery(id+"F0.wireOp",EDGE,"E102"),sQuery(id+"F0.wireOp",EDGE,"E103"),sQuery(id+"F0.wireOp",EDGE,"E104"),sQuery(id+"F0.wireOp",EDGE,"E105"),sQuery(id+"F0.wireOp",EDGE,"E106"),sQuery(id+"F0.wireOp",EDGE,"E107"),sQuery(id+"F0.wireOp",EDGE,"E108"),sQuery(id+"F0.wireOp",EDGE,"E109"),sQuery(id+"F0.wireOp",EDGE,"E110"),sQuery(id+"F0.wireOp",EDGE,"E111"),sQuery(id+"F0.wireOp",EDGE,"E112"),sQuery(id+"F0.wireOp",EDGE,"E113"),sQuery(id+"F0.wireOp",EDGE,"E114"),sQuery(id+"F0.wireOp",EDGE,"E115"),sQuery(id+"F0.wireOp",EDGE,"E116"),sQuery(id+"F0.wireOp",EDGE,"E117"),sQuery(id+"F0.wireOp",EDGE,"E118"),sQuery(id+"F0.wireOp",EDGE,"E119"),sQuery(id+"F0.wireOp",EDGE,"E120"),sQuery(id+"F0.wireOp",EDGE,"E121"),sQuery(id+"F0.wireOp",EDGE,"E122"),sQuery(id+"F0.wireOp",EDGE,"E123"),sQuery(id+"F0.wireOp",EDGE,"E124"),sQuery(id+"F0.wireOp",EDGE,"E125")])],"isStart":false});
            var sketch = newSketch(context, id + "F7", { "sketchPlane" : qUnion([Q0])});
            skLineSegment(sketch, "E151", {"start": v(10.5, -35.27) * mm, "end": v(10.06, -34.1) * mm});
            skLineSegment(sketch, "E152", {"start": v(10.06, -34.1) * mm, "end": v(9.55, -32.8) * mm});
            skLineSegment(sketch, "E153", {"start": v(9.55, -32.8) * mm, "end": v(8.9, -31.57) * mm});
            skLineSegment(sketch, "E154", {"start": v(8.9, -31.57) * mm, "end": v(8.56, -30.4) * mm});
            skLineSegment(sketch, "E155", {"start": v(8.56, -30.4) * mm, "end": v(8.15, -29.23) * mm});
            skLineSegment(sketch, "E156", {"start": v(8.15, -29.23) * mm, "end": v(7.56, -28.06) * mm});
            skLineSegment(sketch, "E157", {"start": v(7.56, -28.06) * mm, "end": v(7.33, -26.42) * mm});
            skLineSegment(sketch, "E158", {"start": v(7.33, -26.42) * mm, "end": v(6.8, -24.83) * mm});
            skLineSegment(sketch, "E159", {"start": v(6.8, -24.83) * mm, "end": v(6.62, -23.43) * mm});
            skLineSegment(sketch, "E160", {"start": v(6.62, -23.43) * mm, "end": v(7.03, -21.55) * mm});
            skLineSegment(sketch, "E161", {"start": v(7.03, -21.55) * mm, "end": v(7.27, -19.24) * mm});
            skLineSegment(sketch, "E162", {"start": v(7.27, -19.24) * mm, "end": v(7.7, -18.53) * mm});
            skLineSegment(sketch, "E163", {"start": v(7.7, -18.53) * mm, "end": v(-2.11, -15.86) * mm});
            skLineSegment(sketch, "E164", {"start": v(-2.11, -15.86) * mm, "end": v(0, -35.44) * mm});
            skLineSegment(sketch, "E165", {"start": v(0, -35.44) * mm, "end": v(10.5, -35.27) * mm});
            skSolve(sketch);
        }
        {
            var Q0;
            Q0=qSketchRegion(id+"F7",true);
            extrude(context, id + "F8", {"entities" : qUnion([Q0]), "operationType" : NewBodyOperationType.REMOVE, "oppositeDirection" : true, "depth" : 25.4 * mm});
        }
        {
            var Q0;
            Q0=makeQuery(id+"F1.opExtrude","CAP_FACE",FACE,{"disambiguationData":[OSD([sQuery(id+"F0.wireOp",EDGE,"E0"),sQuery(id+"F0.wireOp",EDGE,"E1"),sQuery(id+"F0.wireOp",EDGE,"E2"),sQuery(id+"F0.wireOp",EDGE,"E3"),sQuery(id+"F0.wireOp",EDGE,"E4"),sQuery(id+"F0.wireOp",EDGE,"E5"),sQuery(id+"F0.wireOp",EDGE,"E6"),sQuery(id+"F0.wireOp",EDGE,"E7"),sQuery(id+"F0.wireOp",EDGE,"E8"),sQuery(id+"F0.wireOp",EDGE,"E9"),sQuery(id+"F0.wireOp",EDGE,"E10"),sQuery(id+"F0.wireOp",EDGE,"E11"),sQuery(id+"F0.wireOp",EDGE,"E12"),sQuery(id+"F0.wireOp",EDGE,"E13"),sQuery(id+"F0.wireOp",EDGE,"E14"),sQuery(id+"F0.wireOp",EDGE,"E15"),sQuery(id+"F0.wireOp",EDGE,"E16"),sQuery(id+"F0.wireOp",EDGE,"E17"),sQuery(id+"F0.wireOp",EDGE,"E18"),sQuery(id+"F0.wireOp",EDGE,"E19"),sQuery(id+"F0.wireOp",EDGE,"E20"),sQuery(id+"F0.wireOp",EDGE,"E21"),sQuery(id+"F0.wireOp",EDGE,"E22"),sQuery(id+"F0.wireOp",EDGE,"E23"),sQuery(id+"F0.wireOp",EDGE,"E24"),sQuery(id+"F0.wireOp",EDGE,"E25"),sQuery(id+"F0.wireOp",EDGE,"E26"),sQuery(id+"F0.wireOp",EDGE,"E27"),sQuery(id+"F0.wireOp",EDGE,"E28"),sQuery(id+"F0.wireOp",EDGE,"E29"),sQuery(id+"F0.wireOp",EDGE,"E30"),sQuery(id+"F0.wireOp",EDGE,"E31"),sQuery(id+"F0.wireOp",EDGE,"E32"),sQuery(id+"F0.wireOp",EDGE,"E33"),sQuery(id+"F0.wireOp",EDGE,"E34"),sQuery(id+"F0.wireOp",EDGE,"E35"),sQuery(id+"F0.wireOp",EDGE,"E36"),sQuery(id+"F0.wireOp",EDGE,"E37"),sQuery(id+"F0.wireOp",EDGE,"E38"),sQuery(id+"F0.wireOp",EDGE,"E39"),sQuery(id+"F0.wireOp",EDGE,"E40"),sQuery(id+"F0.wireOp",EDGE,"E41"),sQuery(id+"F0.wireOp",EDGE,"E42"),sQuery(id+"F0.wireOp",EDGE,"E43"),sQuery(id+"F0.wireOp",EDGE,"E44"),sQuery(id+"F0.wireOp",EDGE,"E45"),sQuery(id+"F0.wireOp",EDGE,"E46"),sQuery(id+"F0.wireOp",EDGE,"E47"),sQuery(id+"F0.wireOp",EDGE,"E48"),sQuery(id+"F0.wireOp",EDGE,"E49"),sQuery(id+"F0.wireOp",EDGE,"E50"),sQuery(id+"F0.wireOp",EDGE,"E51"),sQuery(id+"F0.wireOp",EDGE,"E52"),sQuery(id+"F0.wireOp",EDGE,"E53"),sQuery(id+"F0.wireOp",EDGE,"E54"),sQuery(id+"F0.wireOp",EDGE,"E55"),sQuery(id+"F0.wireOp",EDGE,"E56"),sQuery(id+"F0.wireOp",EDGE,"E57"),sQuery(id+"F0.wireOp",EDGE,"E58"),sQuery(id+"F0.wireOp",EDGE,"E59"),sQuery(id+"F0.wireOp",EDGE,"E60"),sQuery(id+"F0.wireOp",EDGE,"E61"),sQuery(id+"F0.wireOp",EDGE,"E62"),sQuery(id+"F0.wireOp",EDGE,"E63"),sQuery(id+"F0.wireOp",EDGE,"E64"),sQuery(id+"F0.wireOp",EDGE,"E65"),sQuery(id+"F0.wireOp",EDGE,"E66"),sQuery(id+"F0.wireOp",EDGE,"E67"),sQuery(id+"F0.wireOp",EDGE,"E68"),sQuery(id+"F0.wireOp",EDGE,"E69"),sQuery(id+"F0.wireOp",EDGE,"E70"),sQuery(id+"F0.wireOp",EDGE,"E71"),sQuery(id+"F0.wireOp",EDGE,"E72"),sQuery(id+"F0.wireOp",EDGE,"E73"),sQuery(id+"F0.wireOp",EDGE,"E74"),sQuery(id+"F0.wireOp",EDGE,"E75"),sQuery(id+"F0.wireOp",EDGE,"E76"),sQuery(id+"F0.wireOp",EDGE,"E77"),sQuery(id+"F0.wireOp",EDGE,"E78"),sQuery(id+"F0.wireOp",EDGE,"E79"),sQuery(id+"F0.wireOp",EDGE,"E80"),sQuery(id+"F0.wireOp",EDGE,"E81"),sQuery(id+"F0.wireOp",EDGE,"E82"),sQuery(id+"F0.wireOp",EDGE,"E83"),sQuery(id+"F0.wireOp",EDGE,"E84"),sQuery(id+"F0.wireOp",EDGE,"E85"),sQuery(id+"F0.wireOp",EDGE,"E87"),sQuery(id+"F0.wireOp",EDGE,"E88"),sQuery(id+"F0.wireOp",EDGE,"E89"),sQuery(id+"F0.wireOp",EDGE,"E90"),sQuery(id+"F0.wireOp",EDGE,"E91"),sQuery(id+"F0.wireOp",EDGE,"E92"),sQuery(id+"F0.wireOp",EDGE,"E93"),sQuery(id+"F0.wireOp",EDGE,"E94"),sQuery(id+"F0.wireOp",EDGE,"E95"),sQuery(id+"F0.wireOp",EDGE,"E96"),sQuery(id+"F0.wireOp",EDGE,"E97"),sQuery(id+"F0.wireOp",EDGE,"E98"),sQuery(id+"F0.wireOp",EDGE,"E99"),sQuery(id+"F0.wireOp",EDGE,"E100"),sQuery(id+"F0.wireOp",EDGE,"E101"),sQuery(id+"F0.wireOp",EDGE,"E102"),sQuery(id+"F0.wireOp",EDGE,"E103"),sQuery(id+"F0.wireOp",EDGE,"E104"),sQuery(id+"F0.wireOp",EDGE,"E105"),sQuery(id+"F0.wireOp",EDGE,"E106"),sQuery(id+"F0.wireOp",EDGE,"E107"),sQuery(id+"F0.wireOp",EDGE,"E108"),sQuery(id+"F0.wireOp",EDGE,"E109"),sQuery(id+"F0.wireOp",EDGE,"E110"),sQuery(id+"F0.wireOp",EDGE,"E111"),sQuery(id+"F0.wireOp",EDGE,"E112"),sQuery(id+"F0.wireOp",EDGE,"E113"),sQuery(id+"F0.wireOp",EDGE,"E114"),sQuery(id+"F0.wireOp",EDGE,"E115"),sQuery(id+"F0.wireOp",EDGE,"E116"),sQuery(id+"F0.wireOp",EDGE,"E117"),sQuery(id+"F0.wireOp",EDGE,"E118"),sQuery(id+"F0.wireOp",EDGE,"E119"),sQuery(id+"F0.wireOp",EDGE,"E120"),sQuery(id+"F0.wireOp",EDGE,"E121"),sQuery(id+"F0.wireOp",EDGE,"E122"),sQuery(id+"F0.wireOp",EDGE,"E123"),sQuery(id+"F0.wireOp",EDGE,"E124"),sQuery(id+"F0.wireOp",EDGE,"E125")])],"isStart":false});
            var sketch = newSketch(context, id + "F9", { "sketchPlane" : qUnion([Q0])});
            skLineSegment(sketch, "E166", {"start": v(7.52, -36.4) * mm, "end": v(9.2, -36.08) * mm});
            skLineSegment(sketch, "E167", {"start": v(9.2, -36.08) * mm, "end": v(10.74, -35.7) * mm});
            skLineSegment(sketch, "E168", {"start": v(10.74, -35.7) * mm, "end": v(11.53, -35.07) * mm});
            skLineSegment(sketch, "E169", {"start": v(11.53, -35.07) * mm, "end": v(11.63, -34.12) * mm});
            skLineSegment(sketch, "E170", {"start": v(11.63, -34.12) * mm, "end": v(11.5, -33.15) * mm});
            skLineSegment(sketch, "E171", {"start": v(11.5, -33.15) * mm, "end": v(11.3, -32.17) * mm});
            skLineSegment(sketch, "E172", {"start": v(11.3, -32.17) * mm, "end": v(10.74, -30.62) * mm});
            skLineSegment(sketch, "E173", {"start": v(10.74, -30.62) * mm, "end": v(10.43, -29.6) * mm});
            skLineSegment(sketch, "E174", {"start": v(10.43, -29.6) * mm, "end": v(9.78, -27.95) * mm});
            skLineSegment(sketch, "E175", {"start": v(9.78, -27.95) * mm, "end": v(8.97, -26.34) * mm});
            skLineSegment(sketch, "E176", {"start": v(8.97, -26.34) * mm, "end": v(8.56, -24.97) * mm});
            skLineSegment(sketch, "E177", {"start": v(8.56, -24.97) * mm, "end": v(8.06, -23.35) * mm});
            skLineSegment(sketch, "E178", {"start": v(8.06, -23.35) * mm, "end": v(8.02, -22.32) * mm});
            skLineSegment(sketch, "E179", {"start": v(8.02, -22.32) * mm, "end": v(8.02, -20.62) * mm});
            skLineSegment(sketch, "E180", {"start": v(8.02, -20.62) * mm, "end": v(7.7, -18.53) * mm});
            skLineSegment(sketch, "E181", {"start": v(7.7, -18.53) * mm, "end": v(-0.56, -18.5) * mm});
            skLineSegment(sketch, "E182", {"start": v(-0.56, -18.5) * mm, "end": v(2.22, -31.6) * mm});
            skLineSegment(sketch, "E183", {"start": v(2.22, -31.6) * mm, "end": v(7.52, -36.4) * mm});
            skSolve(sketch);
        }
        {
            var Q0;
            Q0=qSketchRegion(id+"F9",true);
            extrude(context, id + "F10", {"entities" : qUnion([Q0]), "operationType" : NewBodyOperationType.REMOVE, "oppositeDirection" : true, "depth" : 25.4 * mm});
        }
        {
            var Q0;
            Q0=makeQuery(id+"F1.opExtrude","SWEPT_EDGE",EDGE,{"disambiguationData":[OSD([sQuery(id+"F0.wireOp",EDGE,"E91"),sQuery(id+"F0.wireOp",EDGE,"E92")])]});
            var Q1;
            {var subQ0=sQuery(id+"F0.wireOp",EDGE,"E93");var subQ1=sQuery(id+"F0.wireOp",EDGE,"E92");Q1=makeQuery(id+"F6.boolean.opBoolean","MERGE",EDGE,{"derivedFrom":[makeQuery(id+"F1.opExtrude","SWEPT_EDGE",EDGE,{"disambiguationData":[OSD([subQ1,subQ0])]}),makeQuery(id+"F6.opExtrude","SWEPT_EDGE",EDGE,{"disambiguationData":[OSD([subQ1,subQ0,sQuery(id+"F5.wireOp",EDGE,"E147"),sQuery(id+"F5.wireOp",EDGE,"E148")])]})]});}
            var Q2;
            Q2=makeQuery(id+"F6.boolean.opBoolean","COPY",EDGE,{"derivedFrom":makeQuery(id+"F6.opExtrude","SWEPT_EDGE",EDGE,{"disambiguationData":[OSD([sQuery(id+"F5.wireOp",EDGE,"E146"),sQuery(id+"F5.wireOp",EDGE,"E147")])]})});
            var Q3;
            Q3=makeQuery(id+"F6.boolean.opBoolean","COPY",EDGE,{"derivedFrom":makeQuery(id+"F6.opExtrude","SWEPT_EDGE",EDGE,{"disambiguationData":[OSD([sQuery(id+"F5.wireOp",EDGE,"E145"),sQuery(id+"F5.wireOp",EDGE,"E146")])]})});
            var Q4;
            Q4=makeQuery(id+"F6.boolean.opBoolean","COPY",EDGE,{"derivedFrom":makeQuery(id+"F6.opExtrude","SWEPT_EDGE",EDGE,{"disambiguationData":[OSD([sQuery(id+"F5.wireOp",EDGE,"E144"),sQuery(id+"F5.wireOp",EDGE,"E145")])]})});
            var Q5;
            Q5=makeQuery(id+"F6.boolean.opBoolean","COPY",EDGE,{"derivedFrom":makeQuery(id+"F6.opExtrude","SWEPT_EDGE",EDGE,{"disambiguationData":[OSD([sQuery(id+"F5.wireOp",EDGE,"E143"),sQuery(id+"F5.wireOp",EDGE,"E144")])]})});
            var Q6;
            Q6=makeQuery(id+"F6.boolean.opBoolean","COPY",EDGE,{"derivedFrom":makeQuery(id+"F6.opExtrude","SWEPT_EDGE",EDGE,{"disambiguationData":[OSD([sQuery(id+"F5.wireOp",EDGE,"E142"),sQuery(id+"F5.wireOp",EDGE,"E143")])]})});
            var Q7;
            Q7=makeQuery(id+"F6.boolean.opBoolean","COPY",EDGE,{"derivedFrom":makeQuery(id+"F6.opExtrude","SWEPT_EDGE",EDGE,{"disambiguationData":[OSD([sQuery(id+"F5.wireOp",EDGE,"E141"),sQuery(id+"F5.wireOp",EDGE,"E142")])]})});
            var Q8;
            Q8=makeQuery(id+"F6.boolean.opBoolean","COPY",EDGE,{"derivedFrom":makeQuery(id+"F6.opExtrude","SWEPT_EDGE",EDGE,{"disambiguationData":[OSD([sQuery(id+"F5.wireOp",EDGE,"E140"),sQuery(id+"F5.wireOp",EDGE,"E141")])]})});
            var Q9;
            Q9=makeQuery(id+"F6.boolean.opBoolean","COPY",EDGE,{"derivedFrom":makeQuery(id+"F6.opExtrude","SWEPT_EDGE",EDGE,{"disambiguationData":[OSD([sQuery(id+"F5.wireOp",EDGE,"E139"),sQuery(id+"F5.wireOp",EDGE,"E140")])]})});
            var Q10;
            Q10=makeQuery(id+"F6.boolean.opBoolean","COPY",EDGE,{"derivedFrom":makeQuery(id+"F6.opExtrude","SWEPT_EDGE",EDGE,{"disambiguationData":[OSD([sQuery(id+"F5.wireOp",EDGE,"E138"),sQuery(id+"F5.wireOp",EDGE,"E139")])]})});
            var Q11;
            Q11=makeQuery(id+"F6.boolean.opBoolean","COPY",EDGE,{"derivedFrom":makeQuery(id+"F6.opExtrude","SWEPT_EDGE",EDGE,{"disambiguationData":[OSD([sQuery(id+"F5.wireOp",EDGE,"E137"),sQuery(id+"F5.wireOp",EDGE,"E138")])]})});
            var Q12;
            Q12=makeQuery(id+"F6.boolean.opBoolean","COPY",EDGE,{"derivedFrom":makeQuery(id+"F6.opExtrude","SWEPT_EDGE",EDGE,{"disambiguationData":[OSD([sQuery(id+"F5.wireOp",EDGE,"E136"),sQuery(id+"F5.wireOp",EDGE,"E137")])]})});
            var Q13;
            Q13=makeQuery(id+"F6.boolean.opBoolean","COPY",EDGE,{"derivedFrom":makeQuery(id+"F6.opExtrude","SWEPT_EDGE",EDGE,{"disambiguationData":[OSD([sQuery(id+"F5.wireOp",EDGE,"E135"),sQuery(id+"F5.wireOp",EDGE,"E136")])]})});
            var Q14;
            Q14=makeQuery(id+"F6.boolean.opBoolean","COPY",EDGE,{"derivedFrom":makeQuery(id+"F6.opExtrude","SWEPT_EDGE",EDGE,{"disambiguationData":[OSD([sQuery(id+"F5.wireOp",EDGE,"E134"),sQuery(id+"F5.wireOp",EDGE,"E135")])]})});
            var Q15;
            {var subQ0=sQuery(id+"F3.wireOp",EDGE,"E130");var subQ1=sQuery(id+"F3.wireOp",EDGE,"E129");Q15=makeQuery(id+"F6.boolean.opBoolean","MERGE",EDGE,{"derivedFrom":[makeQuery(id+"F4.boolean.opBoolean","COPY",EDGE,{"derivedFrom":makeQuery(id+"F4.opExtrude","SWEPT_EDGE",EDGE,{"disambiguationData":[OSD([subQ1,subQ0])]})}),makeQuery(id+"F6.opExtrude","SWEPT_EDGE",EDGE,{"disambiguationData":[OSD([subQ1,subQ0,sQuery(id+"F5.wireOp",EDGE,"E134"),sQuery(id+"F5.wireOp",EDGE,"E150")])]})]});}
            var Q16;
            Q16=makeQuery(id+"F4.boolean.opBoolean","COPY",EDGE,{"derivedFrom":makeQuery(id+"F4.opExtrude","SWEPT_EDGE",EDGE,{"disambiguationData":[OSD([sQuery(id+"F3.wireOp",EDGE,"E128"),sQuery(id+"F3.wireOp",EDGE,"E129")])]})});
            var Q17;
            Q17=makeQuery(id+"F4.boolean.opBoolean","COPY",EDGE,{"derivedFrom":makeQuery(id+"F4.opExtrude","SWEPT_EDGE",EDGE,{"disambiguationData":[OSD([sQuery(id+"F3.wireOp",EDGE,"E127"),sQuery(id+"F3.wireOp",EDGE,"E128")])]})});
            var Q18;
            Q18=makeQuery(id+"F4.boolean.opBoolean","COPY",EDGE,{"derivedFrom":makeQuery(id+"F4.opExtrude","SWEPT_EDGE",EDGE,{"disambiguationData":[OSD([sQuery(id+"F0.wireOp",EDGE,"E99"),sQuery(id+"F0.wireOp",EDGE,"E100"),sQuery(id+"F0.wireOp",EDGE,"E101"),sQuery(id+"F0.wireOp",EDGE,"E102"),sQuery(id+"F3.wireOp",EDGE,"E126"),sQuery(id+"F3.wireOp",EDGE,"E127")])]})});
            fillet(context, id + "F11", {"entities" : qUnion([Q0, Q1, Q2, Q3, Q4, Q5, Q6, Q7, Q8, Q9, Q10, Q11, Q12, Q13, Q14, Q15, Q16, Q17, Q18]), "radius" : 5.08 * mm, "tangentPropagation" : true, "allowEdgeOverflow" : false});
        }
        {
            var Q0;
            Q0=makeQuery(id+"F1.opExtrude","SWEPT_EDGE",EDGE,{"disambiguationData":[OSD([sQuery(id+"F0.wireOp",EDGE,"E77"),sQuery(id+"F0.wireOp",EDGE,"E78")])]});
            var Q1;
            Q1=makeQuery(id+"F1.opExtrude","SWEPT_EDGE",EDGE,{"disambiguationData":[OSD([sQuery(id+"F0.wireOp",EDGE,"E76"),sQuery(id+"F0.wireOp",EDGE,"E77")])]});
            var Q2;
            Q2=makeQuery(id+"F1.opExtrude","SWEPT_EDGE",EDGE,{"disambiguationData":[OSD([sQuery(id+"F0.wireOp",EDGE,"E75"),sQuery(id+"F0.wireOp",EDGE,"E76")])]});
            var Q3;
            Q3=makeQuery(id+"F1.opExtrude","SWEPT_EDGE",EDGE,{"disambiguationData":[OSD([sQuery(id+"F0.wireOp",EDGE,"E74"),sQuery(id+"F0.wireOp",EDGE,"E75")])]});
            var Q4;
            Q4=makeQuery(id+"F1.opExtrude","SWEPT_EDGE",EDGE,{"disambiguationData":[OSD([sQuery(id+"F0.wireOp",EDGE,"E73"),sQuery(id+"F0.wireOp",EDGE,"E74")])]});
            var Q5;
            Q5=makeQuery(id+"F1.opExtrude","SWEPT_EDGE",EDGE,{"disambiguationData":[OSD([sQuery(id+"F0.wireOp",EDGE,"E72"),sQuery(id+"F0.wireOp",EDGE,"E73")])]});
            var Q6;
            Q6=makeQuery(id+"F1.opExtrude","SWEPT_EDGE",EDGE,{"disambiguationData":[OSD([sQuery(id+"F0.wireOp",EDGE,"E71"),sQuery(id+"F0.wireOp",EDGE,"E72")])]});
            fillet(context, id + "F12", {"entities" : qUnion([Q0, Q1, Q2, Q3, Q4, Q5, Q6]), "radius" : 7.62 * mm, "tangentPropagation" : true, "allowEdgeOverflow" : false});
        }
        {
            var Q0;
            Q0=makeQuery(id+"F1.opExtrude","SWEPT_EDGE",EDGE,{"disambiguationData":[OSD([sQuery(id+"F0.wireOp",EDGE,"E51"),sQuery(id+"F0.wireOp",EDGE,"E52")])]});
            var Q1;
            Q1=makeQuery(id+"F1.opExtrude","SWEPT_EDGE",EDGE,{"disambiguationData":[OSD([sQuery(id+"F0.wireOp",EDGE,"E53"),sQuery(id+"F0.wireOp",EDGE,"E54")])]});
            var Q2;
            Q2=makeQuery(id+"F1.opExtrude","SWEPT_EDGE",EDGE,{"disambiguationData":[OSD([sQuery(id+"F0.wireOp",EDGE,"E49"),sQuery(id+"F0.wireOp",EDGE,"E50")])]});
            var Q3;
            Q3=makeQuery(id+"F1.opExtrude","SWEPT_EDGE",EDGE,{"disambiguationData":[OSD([sQuery(id+"F0.wireOp",EDGE,"E48"),sQuery(id+"F0.wireOp",EDGE,"E49")])]});
            var Q4;
            Q4=makeQuery(id+"F1.opExtrude","SWEPT_EDGE",EDGE,{"disambiguationData":[OSD([sQuery(id+"F0.wireOp",EDGE,"E47"),sQuery(id+"F0.wireOp",EDGE,"E48")])]});
            var Q5;
            Q5=makeQuery(id+"F1.opExtrude","SWEPT_EDGE",EDGE,{"disambiguationData":[OSD([sQuery(id+"F0.wireOp",EDGE,"E55"),sQuery(id+"F0.wireOp",EDGE,"E56")])]});
            var Q6;
            Q6=makeQuery(id+"F1.opExtrude","SWEPT_EDGE",EDGE,{"disambiguationData":[OSD([sQuery(id+"F0.wireOp",EDGE,"E54"),sQuery(id+"F0.wireOp",EDGE,"E55")])]});
            fillet(context, id + "F13", {"entities" : qUnion([Q0, Q1, Q2, Q3, Q4, Q5, Q6]), "radius" : 5.08 * mm, "tangentPropagation" : true, "allowEdgeOverflow" : false});
        }
        {
            var Q0;
            Q0=makeQuery(id+"F1.opExtrude","SWEPT_EDGE",EDGE,{"disambiguationData":[OSD([sQuery(id+"F0.wireOp",EDGE,"E50"),sQuery(id+"F0.wireOp",EDGE,"E51")])]});
            var Q1;
            Q1=makeQuery(id+"F1.opExtrude","SWEPT_EDGE",EDGE,{"disambiguationData":[OSD([sQuery(id+"F0.wireOp",EDGE,"E52"),sQuery(id+"F0.wireOp",EDGE,"E53")])]});
            fillet(context, id + "F14", {"entities" : qUnion([Q0, Q1]), "radius" : 5.08 * mm, "tangentPropagation" : true, "allowEdgeOverflow" : false});
        }
        {
            var Q0;
            Q0=makeQuery(id+"F1.opExtrude","SWEPT_EDGE",EDGE,{"disambiguationData":[OSD([sQuery(id+"F0.wireOp",EDGE,"E3"),sQuery(id+"F0.wireOp",EDGE,"E4")])]});
            var Q1;
            Q1=makeQuery(id+"F1.opExtrude","SWEPT_EDGE",EDGE,{"disambiguationData":[OSD([sQuery(id+"F0.wireOp",EDGE,"E4"),sQuery(id+"F0.wireOp",EDGE,"E5")])]});
            var Q2;
            Q2=makeQuery(id+"F1.opExtrude","SWEPT_EDGE",EDGE,{"disambiguationData":[OSD([sQuery(id+"F0.wireOp",EDGE,"E6"),sQuery(id+"F0.wireOp",EDGE,"E7")])]});
            var Q3;
            Q3=makeQuery(id+"F1.opExtrude","SWEPT_EDGE",EDGE,{"disambiguationData":[OSD([sQuery(id+"F0.wireOp",EDGE,"E7"),sQuery(id+"F0.wireOp",EDGE,"E8")])]});
            var Q4;
            Q4=makeQuery(id+"F1.opExtrude","SWEPT_EDGE",EDGE,{"disambiguationData":[OSD([sQuery(id+"F0.wireOp",EDGE,"E8"),sQuery(id+"F0.wireOp",EDGE,"E9")])]});
            var Q5;
            Q5=makeQuery(id+"F1.opExtrude","SWEPT_EDGE",EDGE,{"disambiguationData":[OSD([sQuery(id+"F0.wireOp",EDGE,"E9"),sQuery(id+"F0.wireOp",EDGE,"E10")])]});
            var Q6;
            Q6=makeQuery(id+"F1.opExtrude","SWEPT_EDGE",EDGE,{"disambiguationData":[OSD([sQuery(id+"F0.wireOp",EDGE,"E10"),sQuery(id+"F0.wireOp",EDGE,"E11")])]});
            var Q7;
            Q7=makeQuery(id+"F1.opExtrude","SWEPT_EDGE",EDGE,{"disambiguationData":[OSD([sQuery(id+"F0.wireOp",EDGE,"E13"),sQuery(id+"F0.wireOp",EDGE,"E14")])]});
            var Q8;
            Q8=makeQuery(id+"F1.opExtrude","SWEPT_EDGE",EDGE,{"disambiguationData":[OSD([sQuery(id+"F0.wireOp",EDGE,"E12"),sQuery(id+"F0.wireOp",EDGE,"E13")])]});
            var Q9;
            Q9=makeQuery(id+"F1.opExtrude","SWEPT_EDGE",EDGE,{"disambiguationData":[OSD([sQuery(id+"F0.wireOp",EDGE,"E15"),sQuery(id+"F0.wireOp",EDGE,"E16")])]});
            var Q10;
            Q10=makeQuery(id+"F1.opExtrude","SWEPT_EDGE",EDGE,{"disambiguationData":[OSD([sQuery(id+"F0.wireOp",EDGE,"E16"),sQuery(id+"F0.wireOp",EDGE,"E17")])]});
            var Q11;
            Q11=makeQuery(id+"F1.opExtrude","SWEPT_EDGE",EDGE,{"disambiguationData":[OSD([sQuery(id+"F0.wireOp",EDGE,"E25"),sQuery(id+"F0.wireOp",EDGE,"E26")])]});
            var Q12;
            Q12=makeQuery(id+"F1.opExtrude","SWEPT_EDGE",EDGE,{"disambiguationData":[OSD([sQuery(id+"F0.wireOp",EDGE,"E26"),sQuery(id+"F0.wireOp",EDGE,"E27")])]});
            var Q13;
            Q13=makeQuery(id+"F1.opExtrude","SWEPT_EDGE",EDGE,{"disambiguationData":[OSD([sQuery(id+"F0.wireOp",EDGE,"E27"),sQuery(id+"F0.wireOp",EDGE,"E28")])]});
            var Q14;
            Q14=makeQuery(id+"F1.opExtrude","SWEPT_EDGE",EDGE,{"disambiguationData":[OSD([sQuery(id+"F0.wireOp",EDGE,"E21"),sQuery(id+"F0.wireOp",EDGE,"E22")])]});
            var Q15;
            Q15=makeQuery(id+"F1.opExtrude","SWEPT_EDGE",EDGE,{"disambiguationData":[OSD([sQuery(id+"F0.wireOp",EDGE,"E19"),sQuery(id+"F0.wireOp",EDGE,"E20")])]});
            var Q16;
            Q16=makeQuery(id+"F1.opExtrude","SWEPT_EDGE",EDGE,{"disambiguationData":[OSD([sQuery(id+"F0.wireOp",EDGE,"E18"),sQuery(id+"F0.wireOp",EDGE,"E19")])]});
            var Q17;
            Q17=makeQuery(id+"F1.opExtrude","SWEPT_EDGE",EDGE,{"disambiguationData":[OSD([sQuery(id+"F0.wireOp",EDGE,"E17"),sQuery(id+"F0.wireOp",EDGE,"E18")])]});
            var Q18;
            Q18=makeQuery(id+"F1.opExtrude","SWEPT_EDGE",EDGE,{"disambiguationData":[OSD([sQuery(id+"F0.wireOp",EDGE,"E20"),sQuery(id+"F0.wireOp",EDGE,"E21")])]});
            var Q19;
            Q19=makeQuery(id+"F1.opExtrude","SWEPT_EDGE",EDGE,{"disambiguationData":[OSD([sQuery(id+"F0.wireOp",EDGE,"E23"),sQuery(id+"F0.wireOp",EDGE,"E24")])]});
            var Q20;
            Q20=makeQuery(id+"F1.opExtrude","SWEPT_EDGE",EDGE,{"disambiguationData":[OSD([sQuery(id+"F0.wireOp",EDGE,"E28"),sQuery(id+"F0.wireOp",EDGE,"E29")])]});
            fillet(context, id + "F15", {"entities" : qUnion([Q0, Q1, Q2, Q3, Q4, Q5, Q6, Q7, Q8, Q9, Q10, Q11, Q12, Q13, Q14, Q15, Q16, Q17, Q18, Q19, Q20]), "radius" : 5.08 * mm, "tangentPropagation" : true, "allowEdgeOverflow" : false});
        }
        {
            var Q0;
            Q0=makeQuery(id+"F1.opExtrude","SWEPT_EDGE",EDGE,{"disambiguationData":[OSD([sQuery(id+"F0.wireOp",EDGE,"E65"),sQuery(id+"F0.wireOp",EDGE,"E66")])]});
            var Q1;
            Q1=makeQuery(id+"F1.opExtrude","SWEPT_EDGE",EDGE,{"disambiguationData":[OSD([sQuery(id+"F0.wireOp",EDGE,"E66"),sQuery(id+"F0.wireOp",EDGE,"E67")])]});
            var Q2;
            Q2=makeQuery(id+"F1.opExtrude","SWEPT_EDGE",EDGE,{"disambiguationData":[OSD([sQuery(id+"F0.wireOp",EDGE,"E87"),sQuery(id+"F0.wireOp",EDGE,"E88")])]});
            var Q3;
            Q3=makeQuery(id+"F1.opExtrude","SWEPT_EDGE",EDGE,{"disambiguationData":[OSD([sQuery(id+"F0.wireOp",EDGE,"E85"),sQuery(id+"F0.wireOp",EDGE,"E87")])]});
            var Q4;
            Q4=makeQuery(id+"F1.opExtrude","SWEPT_EDGE",EDGE,{"disambiguationData":[OSD([sQuery(id+"F0.wireOp",EDGE,"E84"),sQuery(id+"F0.wireOp",EDGE,"E85")])]});
            var Q5;
            Q5=makeQuery(id+"F1.opExtrude","SWEPT_EDGE",EDGE,{"disambiguationData":[OSD([sQuery(id+"F0.wireOp",EDGE,"E37"),sQuery(id+"F0.wireOp",EDGE,"E38")])]});
            var Q6;
            Q6=makeQuery(id+"F1.opExtrude","SWEPT_EDGE",EDGE,{"disambiguationData":[OSD([sQuery(id+"F0.wireOp",EDGE,"E35"),sQuery(id+"F0.wireOp",EDGE,"E36")])]});
            var Q7;
            Q7=makeQuery(id+"F1.opExtrude","SWEPT_EDGE",EDGE,{"disambiguationData":[OSD([sQuery(id+"F0.wireOp",EDGE,"E22"),sQuery(id+"F0.wireOp",EDGE,"E23")])]});
            fillet(context, id + "F16", {"entities" : qUnion([Q0, Q1, Q2, Q3, Q4, Q5, Q6, Q7]), "radius" : 1.27 * mm, "tangentPropagation" : true, "allowEdgeOverflow" : false});
        }
        {
            var Q0;
            Q0=makeQuery(id+"F1.opExtrude","CAP_FACE",FACE,{"disambiguationData":[OSD([sQuery(id+"F0.wireOp",EDGE,"E0"),sQuery(id+"F0.wireOp",EDGE,"E1"),sQuery(id+"F0.wireOp",EDGE,"E2"),sQuery(id+"F0.wireOp",EDGE,"E3"),sQuery(id+"F0.wireOp",EDGE,"E4"),sQuery(id+"F0.wireOp",EDGE,"E5"),sQuery(id+"F0.wireOp",EDGE,"E6"),sQuery(id+"F0.wireOp",EDGE,"E7"),sQuery(id+"F0.wireOp",EDGE,"E8"),sQuery(id+"F0.wireOp",EDGE,"E9"),sQuery(id+"F0.wireOp",EDGE,"E10"),sQuery(id+"F0.wireOp",EDGE,"E11"),sQuery(id+"F0.wireOp",EDGE,"E12"),sQuery(id+"F0.wireOp",EDGE,"E13"),sQuery(id+"F0.wireOp",EDGE,"E14"),sQuery(id+"F0.wireOp",EDGE,"E15"),sQuery(id+"F0.wireOp",EDGE,"E16"),sQuery(id+"F0.wireOp",EDGE,"E17"),sQuery(id+"F0.wireOp",EDGE,"E18"),sQuery(id+"F0.wireOp",EDGE,"E19"),sQuery(id+"F0.wireOp",EDGE,"E20"),sQuery(id+"F0.wireOp",EDGE,"E21"),sQuery(id+"F0.wireOp",EDGE,"E22"),sQuery(id+"F0.wireOp",EDGE,"E23"),sQuery(id+"F0.wireOp",EDGE,"E24"),sQuery(id+"F0.wireOp",EDGE,"E25"),sQuery(id+"F0.wireOp",EDGE,"E26"),sQuery(id+"F0.wireOp",EDGE,"E27"),sQuery(id+"F0.wireOp",EDGE,"E28"),sQuery(id+"F0.wireOp",EDGE,"E29"),sQuery(id+"F0.wireOp",EDGE,"E30"),sQuery(id+"F0.wireOp",EDGE,"E31"),sQuery(id+"F0.wireOp",EDGE,"E32"),sQuery(id+"F0.wireOp",EDGE,"E33"),sQuery(id+"F0.wireOp",EDGE,"E34"),sQuery(id+"F0.wireOp",EDGE,"E35"),sQuery(id+"F0.wireOp",EDGE,"E36"),sQuery(id+"F0.wireOp",EDGE,"E37"),sQuery(id+"F0.wireOp",EDGE,"E38"),sQuery(id+"F0.wireOp",EDGE,"E39"),sQuery(id+"F0.wireOp",EDGE,"E40"),sQuery(id+"F0.wireOp",EDGE,"E41"),sQuery(id+"F0.wireOp",EDGE,"E42"),sQuery(id+"F0.wireOp",EDGE,"E43"),sQuery(id+"F0.wireOp",EDGE,"E44"),sQuery(id+"F0.wireOp",EDGE,"E45"),sQuery(id+"F0.wireOp",EDGE,"E46"),sQuery(id+"F0.wireOp",EDGE,"E47"),sQuery(id+"F0.wireOp",EDGE,"E48"),sQuery(id+"F0.wireOp",EDGE,"E49"),sQuery(id+"F0.wireOp",EDGE,"E50"),sQuery(id+"F0.wireOp",EDGE,"E51"),sQuery(id+"F0.wireOp",EDGE,"E52"),sQuery(id+"F0.wireOp",EDGE,"E53"),sQuery(id+"F0.wireOp",EDGE,"E54"),sQuery(id+"F0.wireOp",EDGE,"E55"),sQuery(id+"F0.wireOp",EDGE,"E56"),sQuery(id+"F0.wireOp",EDGE,"E57"),sQuery(id+"F0.wireOp",EDGE,"E58"),sQuery(id+"F0.wireOp",EDGE,"E59"),sQuery(id+"F0.wireOp",EDGE,"E60"),sQuery(id+"F0.wireOp",EDGE,"E61"),sQuery(id+"F0.wireOp",EDGE,"E62"),sQuery(id+"F0.wireOp",EDGE,"E63"),sQuery(id+"F0.wireOp",EDGE,"E64"),sQuery(id+"F0.wireOp",EDGE,"E65"),sQuery(id+"F0.wireOp",EDGE,"E66"),sQuery(id+"F0.wireOp",EDGE,"E67"),sQuery(id+"F0.wireOp",EDGE,"E68"),sQuery(id+"F0.wireOp",EDGE,"E69"),sQuery(id+"F0.wireOp",EDGE,"E70"),sQuery(id+"F0.wireOp",EDGE,"E71"),sQuery(id+"F0.wireOp",EDGE,"E72"),sQuery(id+"F0.wireOp",EDGE,"E73"),sQuery(id+"F0.wireOp",EDGE,"E74"),sQuery(id+"F0.wireOp",EDGE,"E75"),sQuery(id+"F0.wireOp",EDGE,"E76"),sQuery(id+"F0.wireOp",EDGE,"E77"),sQuery(id+"F0.wireOp",EDGE,"E78"),sQuery(id+"F0.wireOp",EDGE,"E79"),sQuery(id+"F0.wireOp",EDGE,"E80"),sQuery(id+"F0.wireOp",EDGE,"E81"),sQuery(id+"F0.wireOp",EDGE,"E82"),sQuery(id+"F0.wireOp",EDGE,"E83"),sQuery(id+"F0.wireOp",EDGE,"E84"),sQuery(id+"F0.wireOp",EDGE,"E85"),sQuery(id+"F0.wireOp",EDGE,"E87"),sQuery(id+"F0.wireOp",EDGE,"E88"),sQuery(id+"F0.wireOp",EDGE,"E89"),sQuery(id+"F0.wireOp",EDGE,"E90"),sQuery(id+"F0.wireOp",EDGE,"E91"),sQuery(id+"F0.wireOp",EDGE,"E92"),sQuery(id+"F0.wireOp",EDGE,"E93"),sQuery(id+"F0.wireOp",EDGE,"E94"),sQuery(id+"F0.wireOp",EDGE,"E95"),sQuery(id+"F0.wireOp",EDGE,"E96"),sQuery(id+"F0.wireOp",EDGE,"E97"),sQuery(id+"F0.wireOp",EDGE,"E98"),sQuery(id+"F0.wireOp",EDGE,"E99"),sQuery(id+"F0.wireOp",EDGE,"E100"),sQuery(id+"F0.wireOp",EDGE,"E101"),sQuery(id+"F0.wireOp",EDGE,"E102"),sQuery(id+"F0.wireOp",EDGE,"E103"),sQuery(id+"F0.wireOp",EDGE,"E104"),sQuery(id+"F0.wireOp",EDGE,"E105"),sQuery(id+"F0.wireOp",EDGE,"E106"),sQuery(id+"F0.wireOp",EDGE,"E107"),sQuery(id+"F0.wireOp",EDGE,"E108"),sQuery(id+"F0.wireOp",EDGE,"E109"),sQuery(id+"F0.wireOp",EDGE,"E110"),sQuery(id+"F0.wireOp",EDGE,"E111"),sQuery(id+"F0.wireOp",EDGE,"E112"),sQuery(id+"F0.wireOp",EDGE,"E113"),sQuery(id+"F0.wireOp",EDGE,"E114"),sQuery(id+"F0.wireOp",EDGE,"E115"),sQuery(id+"F0.wireOp",EDGE,"E116"),sQuery(id+"F0.wireOp",EDGE,"E117"),sQuery(id+"F0.wireOp",EDGE,"E118"),sQuery(id+"F0.wireOp",EDGE,"E119"),sQuery(id+"F0.wireOp",EDGE,"E120"),sQuery(id+"F0.wireOp",EDGE,"E121"),sQuery(id+"F0.wireOp",EDGE,"E122"),sQuery(id+"F0.wireOp",EDGE,"E123"),sQuery(id+"F0.wireOp",EDGE,"E124"),sQuery(id+"F0.wireOp",EDGE,"E125")])],"isStart":false});
            var sketch = newSketch(context, id + "F17", { "sketchPlane" : qUnion([Q0])});
            skLineSegment(sketch, "E184", {"start": v(-63, -11.45) * mm, "end": v(-60.72, -9.95) * mm});
            skLineSegment(sketch, "E185", {"start": v(-60.72, -9.95) * mm, "end": v(-57.73, -8.63) * mm});
            skLineSegment(sketch, "E186", {"start": v(-57.73, -8.63) * mm, "end": v(-54.86, -7.96) * mm});
            skLineSegment(sketch, "E187", {"start": v(-54.86, -7.96) * mm, "end": v(-51.1, -7.96) * mm});
            skLineSegment(sketch, "E188", {"start": v(-51.1, -7.96) * mm, "end": v(-43.57, -9.07) * mm});
            skLineSegment(sketch, "E189", {"start": v(-43.57, -9.07) * mm, "end": v(-39.92, -9.51) * mm});
            skLineSegment(sketch, "E190", {"start": v(-39.92, -9.51) * mm, "end": v(-35.93, -9.73) * mm});
            skLineSegment(sketch, "E191", {"start": v(-35.93, -9.73) * mm, "end": v(-31.29, -10.06) * mm});
            skLineSegment(sketch, "E192", {"start": v(-31.29, -10.06) * mm, "end": v(-27.77, -10.44) * mm});
            skLineSegment(sketch, "E193", {"start": v(-27.77, -10.44) * mm, "end": v(-26.22, -22.14) * mm});
            skLineSegment(sketch, "E194", {"start": v(-26.22, -22.14) * mm, "end": v(-52.07, -61.66) * mm});
            skLineSegment(sketch, "E195", {"start": v(-52.07, -61.66) * mm, "end": v(-112.78, -54.57) * mm});
            skLineSegment(sketch, "E196", {"start": v(-112.78, -54.57) * mm, "end": v(-88.26, -27.1) * mm});
            skLineSegment(sketch, "E197", {"start": v(-88.26, -27.1) * mm, "end": v(-63, -11.45) * mm});
            skSolve(sketch);
        }
        {
            var Q0;
            Q0=qSketchRegion(id+"F17",true);
            extrude(context, id + "F18", {"entities" : qUnion([Q0]), "operationType" : NewBodyOperationType.REMOVE, "oppositeDirection" : true, "depth" : 2.54 * mm});
        }
        {
            var Q0;
            Q0=makeQuery(id+"F1.opExtrude","CAP_FACE",FACE,{"disambiguationData":[OSD([sQuery(id+"F0.wireOp",EDGE,"E0"),sQuery(id+"F0.wireOp",EDGE,"E1"),sQuery(id+"F0.wireOp",EDGE,"E2"),sQuery(id+"F0.wireOp",EDGE,"E3"),sQuery(id+"F0.wireOp",EDGE,"E4"),sQuery(id+"F0.wireOp",EDGE,"E5"),sQuery(id+"F0.wireOp",EDGE,"E6"),sQuery(id+"F0.wireOp",EDGE,"E7"),sQuery(id+"F0.wireOp",EDGE,"E8"),sQuery(id+"F0.wireOp",EDGE,"E9"),sQuery(id+"F0.wireOp",EDGE,"E10"),sQuery(id+"F0.wireOp",EDGE,"E11"),sQuery(id+"F0.wireOp",EDGE,"E12"),sQuery(id+"F0.wireOp",EDGE,"E13"),sQuery(id+"F0.wireOp",EDGE,"E14"),sQuery(id+"F0.wireOp",EDGE,"E15"),sQuery(id+"F0.wireOp",EDGE,"E16"),sQuery(id+"F0.wireOp",EDGE,"E17"),sQuery(id+"F0.wireOp",EDGE,"E18"),sQuery(id+"F0.wireOp",EDGE,"E19"),sQuery(id+"F0.wireOp",EDGE,"E20"),sQuery(id+"F0.wireOp",EDGE,"E21"),sQuery(id+"F0.wireOp",EDGE,"E22"),sQuery(id+"F0.wireOp",EDGE,"E23"),sQuery(id+"F0.wireOp",EDGE,"E24"),sQuery(id+"F0.wireOp",EDGE,"E25"),sQuery(id+"F0.wireOp",EDGE,"E26"),sQuery(id+"F0.wireOp",EDGE,"E27"),sQuery(id+"F0.wireOp",EDGE,"E28"),sQuery(id+"F0.wireOp",EDGE,"E29"),sQuery(id+"F0.wireOp",EDGE,"E30"),sQuery(id+"F0.wireOp",EDGE,"E31"),sQuery(id+"F0.wireOp",EDGE,"E32"),sQuery(id+"F0.wireOp",EDGE,"E33"),sQuery(id+"F0.wireOp",EDGE,"E34"),sQuery(id+"F0.wireOp",EDGE,"E35"),sQuery(id+"F0.wireOp",EDGE,"E36"),sQuery(id+"F0.wireOp",EDGE,"E37"),sQuery(id+"F0.wireOp",EDGE,"E38"),sQuery(id+"F0.wireOp",EDGE,"E39"),sQuery(id+"F0.wireOp",EDGE,"E40"),sQuery(id+"F0.wireOp",EDGE,"E41"),sQuery(id+"F0.wireOp",EDGE,"E42"),sQuery(id+"F0.wireOp",EDGE,"E43"),sQuery(id+"F0.wireOp",EDGE,"E44"),sQuery(id+"F0.wireOp",EDGE,"E45"),sQuery(id+"F0.wireOp",EDGE,"E46"),sQuery(id+"F0.wireOp",EDGE,"E47"),sQuery(id+"F0.wireOp",EDGE,"E48"),sQuery(id+"F0.wireOp",EDGE,"E49"),sQuery(id+"F0.wireOp",EDGE,"E50"),sQuery(id+"F0.wireOp",EDGE,"E51"),sQuery(id+"F0.wireOp",EDGE,"E52"),sQuery(id+"F0.wireOp",EDGE,"E53"),sQuery(id+"F0.wireOp",EDGE,"E54"),sQuery(id+"F0.wireOp",EDGE,"E55"),sQuery(id+"F0.wireOp",EDGE,"E56"),sQuery(id+"F0.wireOp",EDGE,"E57"),sQuery(id+"F0.wireOp",EDGE,"E58"),sQuery(id+"F0.wireOp",EDGE,"E59"),sQuery(id+"F0.wireOp",EDGE,"E60"),sQuery(id+"F0.wireOp",EDGE,"E61"),sQuery(id+"F0.wireOp",EDGE,"E62"),sQuery(id+"F0.wireOp",EDGE,"E63"),sQuery(id+"F0.wireOp",EDGE,"E64"),sQuery(id+"F0.wireOp",EDGE,"E65"),sQuery(id+"F0.wireOp",EDGE,"E66"),sQuery(id+"F0.wireOp",EDGE,"E67"),sQuery(id+"F0.wireOp",EDGE,"E68"),sQuery(id+"F0.wireOp",EDGE,"E69"),sQuery(id+"F0.wireOp",EDGE,"E70"),sQuery(id+"F0.wireOp",EDGE,"E71"),sQuery(id+"F0.wireOp",EDGE,"E72"),sQuery(id+"F0.wireOp",EDGE,"E73"),sQuery(id+"F0.wireOp",EDGE,"E74"),sQuery(id+"F0.wireOp",EDGE,"E75"),sQuery(id+"F0.wireOp",EDGE,"E76"),sQuery(id+"F0.wireOp",EDGE,"E77"),sQuery(id+"F0.wireOp",EDGE,"E78"),sQuery(id+"F0.wireOp",EDGE,"E79"),sQuery(id+"F0.wireOp",EDGE,"E80"),sQuery(id+"F0.wireOp",EDGE,"E81"),sQuery(id+"F0.wireOp",EDGE,"E82"),sQuery(id+"F0.wireOp",EDGE,"E83"),sQuery(id+"F0.wireOp",EDGE,"E84"),sQuery(id+"F0.wireOp",EDGE,"E85"),sQuery(id+"F0.wireOp",EDGE,"E87"),sQuery(id+"F0.wireOp",EDGE,"E88"),sQuery(id+"F0.wireOp",EDGE,"E89"),sQuery(id+"F0.wireOp",EDGE,"E90"),sQuery(id+"F0.wireOp",EDGE,"E91"),sQuery(id+"F0.wireOp",EDGE,"E92"),sQuery(id+"F0.wireOp",EDGE,"E93"),sQuery(id+"F0.wireOp",EDGE,"E94"),sQuery(id+"F0.wireOp",EDGE,"E95"),sQuery(id+"F0.wireOp",EDGE,"E96"),sQuery(id+"F0.wireOp",EDGE,"E97"),sQuery(id+"F0.wireOp",EDGE,"E98"),sQuery(id+"F0.wireOp",EDGE,"E99"),sQuery(id+"F0.wireOp",EDGE,"E100"),sQuery(id+"F0.wireOp",EDGE,"E101"),sQuery(id+"F0.wireOp",EDGE,"E102"),sQuery(id+"F0.wireOp",EDGE,"E103"),sQuery(id+"F0.wireOp",EDGE,"E104"),sQuery(id+"F0.wireOp",EDGE,"E105"),sQuery(id+"F0.wireOp",EDGE,"E106"),sQuery(id+"F0.wireOp",EDGE,"E107"),sQuery(id+"F0.wireOp",EDGE,"E108"),sQuery(id+"F0.wireOp",EDGE,"E109"),sQuery(id+"F0.wireOp",EDGE,"E110"),sQuery(id+"F0.wireOp",EDGE,"E111"),sQuery(id+"F0.wireOp",EDGE,"E112"),sQuery(id+"F0.wireOp",EDGE,"E113"),sQuery(id+"F0.wireOp",EDGE,"E114"),sQuery(id+"F0.wireOp",EDGE,"E115"),sQuery(id+"F0.wireOp",EDGE,"E116"),sQuery(id+"F0.wireOp",EDGE,"E117"),sQuery(id+"F0.wireOp",EDGE,"E118"),sQuery(id+"F0.wireOp",EDGE,"E119"),sQuery(id+"F0.wireOp",EDGE,"E120"),sQuery(id+"F0.wireOp",EDGE,"E121"),sQuery(id+"F0.wireOp",EDGE,"E122"),sQuery(id+"F0.wireOp",EDGE,"E123"),sQuery(id+"F0.wireOp",EDGE,"E124"),sQuery(id+"F0.wireOp",EDGE,"E125")])],"isStart":false});
            var sketch = newSketch(context, id + "F19", { "sketchPlane" : qUnion([Q0])});
            skLineSegment(sketch, "E198", {"start": v(7.7, -14.43) * mm, "end": v(10.6, -13.3) * mm});
            skLineSegment(sketch, "E199", {"start": v(10.6, -13.3) * mm, "end": v(12.75, -13.06) * mm});
            skLineSegment(sketch, "E200", {"start": v(12.75, -13.06) * mm, "end": v(15.1, -12.88) * mm});
            skLineSegment(sketch, "E201", {"start": v(15.1, -12.88) * mm, "end": v(17.52, -12.68) * mm});
            skLineSegment(sketch, "E202", {"start": v(17.52, -12.68) * mm, "end": v(21.5, -12.68) * mm});
            skLineSegment(sketch, "E203", {"start": v(21.5, -12.68) * mm, "end": v(23.7, -13) * mm});
            skLineSegment(sketch, "E204", {"start": v(23.7, -13) * mm, "end": v(27.14, -13) * mm});
            skLineSegment(sketch, "E205", {"start": v(27.14, -13) * mm, "end": v(31.64, -13.75) * mm});
            skLineSegment(sketch, "E206", {"start": v(31.64, -13.75) * mm, "end": v(36.27, -15.18) * mm});
            skLineSegment(sketch, "E207", {"start": v(36.27, -15.18) * mm, "end": v(39, -15.37) * mm});
            skLineSegment(sketch, "E208", {"start": v(39, -15.37) * mm, "end": v(41.4, -16.85) * mm});
            skLineSegment(sketch, "E209", {"start": v(41.4, -16.85) * mm, "end": v(47.15, -51.46) * mm});
            skLineSegment(sketch, "E210", {"start": v(47.15, -51.46) * mm, "end": v(-3.17, -68.67) * mm});
            skLineSegment(sketch, "E211", {"start": v(-3.17, -68.67) * mm, "end": v(-29.86, -45.84) * mm});
            skLineSegment(sketch, "E212", {"start": v(-29.86, -45.84) * mm, "end": v(7.7, -14.43) * mm});
            skSolve(sketch);
        }
        {
            var Q0;
            Q0=qSketchRegion(id+"F19",true);
            extrude(context, id + "F20", {"entities" : qUnion([Q0]), "operationType" : NewBodyOperationType.REMOVE, "oppositeDirection" : true, "depth" : 2.54 * mm});
        }
        {
            var Q0;
            Q0=makeQuery(id+"F18.boolean.opBoolean","COPY",EDGE,{"derivedFrom":makeQuery(id+"F18.opExtrude","SWEPT_EDGE",EDGE,{"disambiguationData":[OSD([sQuery(id+"F17.wireOp",EDGE,"E185"),sQuery(id+"F17.wireOp",EDGE,"E186")])]})});
            var Q1;
            Q1=makeQuery(id+"F18.boolean.opBoolean","COPY",EDGE,{"derivedFrom":makeQuery(id+"F18.opExtrude","SWEPT_EDGE",EDGE,{"disambiguationData":[OSD([sQuery(id+"F17.wireOp",EDGE,"E186"),sQuery(id+"F17.wireOp",EDGE,"E187")])]})});
            var Q2;
            Q2=makeQuery(id+"F18.boolean.opBoolean","COPY",EDGE,{"derivedFrom":makeQuery(id+"F18.opExtrude","SWEPT_EDGE",EDGE,{"disambiguationData":[OSD([sQuery(id+"F17.wireOp",EDGE,"E187"),sQuery(id+"F17.wireOp",EDGE,"E188")])]})});
            var Q3;
            Q3=makeQuery(id+"F18.boolean.opBoolean","COPY",EDGE,{"derivedFrom":makeQuery(id+"F18.opExtrude","SWEPT_EDGE",EDGE,{"disambiguationData":[OSD([sQuery(id+"F17.wireOp",EDGE,"E188"),sQuery(id+"F17.wireOp",EDGE,"E189")])]})});
            var Q4;
            Q4=makeQuery(id+"F18.boolean.opBoolean","COPY",EDGE,{"derivedFrom":makeQuery(id+"F18.opExtrude","SWEPT_EDGE",EDGE,{"disambiguationData":[OSD([sQuery(id+"F17.wireOp",EDGE,"E189"),sQuery(id+"F17.wireOp",EDGE,"E190")])]})});
            var Q5;
            Q5=makeQuery(id+"F18.boolean.opBoolean","COPY",EDGE,{"derivedFrom":makeQuery(id+"F18.opExtrude","SWEPT_EDGE",EDGE,{"disambiguationData":[OSD([sQuery(id+"F17.wireOp",EDGE,"E190"),sQuery(id+"F17.wireOp",EDGE,"E191")])]})});
            var Q6;
            Q6=makeQuery(id+"F18.boolean.opBoolean","COPY",EDGE,{"derivedFrom":makeQuery(id+"F18.opExtrude","SWEPT_EDGE",EDGE,{"disambiguationData":[OSD([sQuery(id+"F17.wireOp",EDGE,"E191"),sQuery(id+"F17.wireOp",EDGE,"E192")])]})});
            var Q7;
            {var subQ0=sQuery(id+"F0.wireOp",EDGE,"E49");var subQ1=sQuery(id+"F0.wireOp",EDGE,"E48");Q7=makeQuery(id+"F18.boolean.opBoolean","MERGE",EDGE,{"derivedFrom":[makeQuery(id+"F13.opFillet","BLEND_EDGE",EDGE,{"blendedFrom":[makeQuery(id+"F1.opExtrude","SWEPT_EDGE",EDGE,{"disambiguationData":[OSD([subQ1,subQ0])]}),makeQuery(id+"F1.opExtrude","SWEPT_FACE",FACE,{"disambiguationData":[OSD([subQ0])]})],"blendedInto":[makeQuery(id+"F1.opExtrude","SWEPT_FACE",FACE,{"disambiguationData":[OSD([subQ0])]})]}),makeQuery(id+"F18.opExtrude","SWEPT_EDGE",EDGE,{"disambiguationData":[OSD([sQuery(id+"F0.wireOp",EDGE,"E0"),sQuery(id+"F0.wireOp",EDGE,"E1"),sQuery(id+"F0.wireOp",EDGE,"E2"),sQuery(id+"F0.wireOp",EDGE,"E3"),sQuery(id+"F0.wireOp",EDGE,"E4"),sQuery(id+"F0.wireOp",EDGE,"E5"),sQuery(id+"F0.wireOp",EDGE,"E6"),sQuery(id+"F0.wireOp",EDGE,"E7"),sQuery(id+"F0.wireOp",EDGE,"E8"),sQuery(id+"F0.wireOp",EDGE,"E9"),sQuery(id+"F0.wireOp",EDGE,"E10"),sQuery(id+"F0.wireOp",EDGE,"E11"),sQuery(id+"F0.wireOp",EDGE,"E12"),sQuery(id+"F0.wireOp",EDGE,"E13"),sQuery(id+"F0.wireOp",EDGE,"E14"),sQuery(id+"F0.wireOp",EDGE,"E15"),sQuery(id+"F0.wireOp",EDGE,"E16"),sQuery(id+"F0.wireOp",EDGE,"E17"),sQuery(id+"F0.wireOp",EDGE,"E18"),sQuery(id+"F0.wireOp",EDGE,"E19"),sQuery(id+"F0.wireOp",EDGE,"E20"),sQuery(id+"F0.wireOp",EDGE,"E21"),sQuery(id+"F0.wireOp",EDGE,"E22"),sQuery(id+"F0.wireOp",EDGE,"E23"),sQuery(id+"F0.wireOp",EDGE,"E24"),sQuery(id+"F0.wireOp",EDGE,"E25"),sQuery(id+"F0.wireOp",EDGE,"E26"),sQuery(id+"F0.wireOp",EDGE,"E27"),sQuery(id+"F0.wireOp",EDGE,"E28"),sQuery(id+"F0.wireOp",EDGE,"E29"),sQuery(id+"F0.wireOp",EDGE,"E30"),sQuery(id+"F0.wireOp",EDGE,"E31"),sQuery(id+"F0.wireOp",EDGE,"E32"),sQuery(id+"F0.wireOp",EDGE,"E33"),sQuery(id+"F0.wireOp",EDGE,"E34"),sQuery(id+"F0.wireOp",EDGE,"E35"),sQuery(id+"F0.wireOp",EDGE,"E36"),sQuery(id+"F0.wireOp",EDGE,"E37"),sQuery(id+"F0.wireOp",EDGE,"E38"),sQuery(id+"F0.wireOp",EDGE,"E39"),sQuery(id+"F0.wireOp",EDGE,"E40"),sQuery(id+"F0.wireOp",EDGE,"E41"),sQuery(id+"F0.wireOp",EDGE,"E42"),sQuery(id+"F0.wireOp",EDGE,"E43"),sQuery(id+"F0.wireOp",EDGE,"E44"),sQuery(id+"F0.wireOp",EDGE,"E45"),sQuery(id+"F0.wireOp",EDGE,"E46"),sQuery(id+"F0.wireOp",EDGE,"E47"),subQ1,subQ0,sQuery(id+"F0.wireOp",EDGE,"E50"),sQuery(id+"F0.wireOp",EDGE,"E51"),sQuery(id+"F0.wireOp",EDGE,"E52"),sQuery(id+"F0.wireOp",EDGE,"E53"),sQuery(id+"F0.wireOp",EDGE,"E54"),sQuery(id+"F0.wireOp",EDGE,"E55"),sQuery(id+"F0.wireOp",EDGE,"E56"),sQuery(id+"F0.wireOp",EDGE,"E57"),sQuery(id+"F0.wireOp",EDGE,"E58"),sQuery(id+"F0.wireOp",EDGE,"E59"),sQuery(id+"F0.wireOp",EDGE,"E60"),sQuery(id+"F0.wireOp",EDGE,"E61"),sQuery(id+"F0.wireOp",EDGE,"E62"),sQuery(id+"F0.wireOp",EDGE,"E63"),sQuery(id+"F0.wireOp",EDGE,"E64"),sQuery(id+"F0.wireOp",EDGE,"E65"),sQuery(id+"F0.wireOp",EDGE,"E66"),sQuery(id+"F0.wireOp",EDGE,"E67"),sQuery(id+"F0.wireOp",EDGE,"E68"),sQuery(id+"F0.wireOp",EDGE,"E69"),sQuery(id+"F0.wireOp",EDGE,"E70"),sQuery(id+"F0.wireOp",EDGE,"E71"),sQuery(id+"F0.wireOp",EDGE,"E72"),sQuery(id+"F0.wireOp",EDGE,"E73"),sQuery(id+"F0.wireOp",EDGE,"E74"),sQuery(id+"F0.wireOp",EDGE,"E75"),sQuery(id+"F0.wireOp",EDGE,"E76"),sQuery(id+"F0.wireOp",EDGE,"E77"),sQuery(id+"F0.wireOp",EDGE,"E78"),sQuery(id+"F0.wireOp",EDGE,"E79"),sQuery(id+"F0.wireOp",EDGE,"E80"),sQuery(id+"F0.wireOp",EDGE,"E81"),sQuery(id+"F0.wireOp",EDGE,"E82"),sQuery(id+"F0.wireOp",EDGE,"E83"),sQuery(id+"F0.wireOp",EDGE,"E84"),sQuery(id+"F0.wireOp",EDGE,"E85"),sQuery(id+"F0.wireOp",EDGE,"E87"),sQuery(id+"F0.wireOp",EDGE,"E88"),sQuery(id+"F0.wireOp",EDGE,"E89"),sQuery(id+"F0.wireOp",EDGE,"E90"),sQuery(id+"F0.wireOp",EDGE,"E91"),sQuery(id+"F0.wireOp",EDGE,"E92"),sQuery(id+"F0.wireOp",EDGE,"E93"),sQuery(id+"F0.wireOp",EDGE,"E94"),sQuery(id+"F0.wireOp",EDGE,"E95"),sQuery(id+"F0.wireOp",EDGE,"E96"),sQuery(id+"F0.wireOp",EDGE,"E97"),sQuery(id+"F0.wireOp",EDGE,"E98"),sQuery(id+"F0.wireOp",EDGE,"E99"),sQuery(id+"F0.wireOp",EDGE,"E100"),sQuery(id+"F0.wireOp",EDGE,"E101"),sQuery(id+"F0.wireOp",EDGE,"E102"),sQuery(id+"F0.wireOp",EDGE,"E103"),sQuery(id+"F0.wireOp",EDGE,"E104"),sQuery(id+"F0.wireOp",EDGE,"E105"),sQuery(id+"F0.wireOp",EDGE,"E106"),sQuery(id+"F0.wireOp",EDGE,"E107"),sQuery(id+"F0.wireOp",EDGE,"E108"),sQuery(id+"F0.wireOp",EDGE,"E109"),sQuery(id+"F0.wireOp",EDGE,"E110"),sQuery(id+"F0.wireOp",EDGE,"E111"),sQuery(id+"F0.wireOp",EDGE,"E112"),sQuery(id+"F0.wireOp",EDGE,"E113"),sQuery(id+"F0.wireOp",EDGE,"E114"),sQuery(id+"F0.wireOp",EDGE,"E115"),sQuery(id+"F0.wireOp",EDGE,"E116"),sQuery(id+"F0.wireOp",EDGE,"E117"),sQuery(id+"F0.wireOp",EDGE,"E118"),sQuery(id+"F0.wireOp",EDGE,"E119"),sQuery(id+"F0.wireOp",EDGE,"E120"),sQuery(id+"F0.wireOp",EDGE,"E121"),sQuery(id+"F0.wireOp",EDGE,"E122"),sQuery(id+"F0.wireOp",EDGE,"E123"),sQuery(id+"F0.wireOp",EDGE,"E124"),sQuery(id+"F0.wireOp",EDGE,"E125"),sQuery(id+"F17.wireOp",EDGE,"E192"),sQuery(id+"F17.wireOp",EDGE,"E193")])]})]});}
            var Q8;
            Q8=makeQuery(id+"F18.boolean.opBoolean","COPY",EDGE,{"derivedFrom":makeQuery(id+"F18.opExtrude","SWEPT_EDGE",EDGE,{"disambiguationData":[OSD([sQuery(id+"F17.wireOp",EDGE,"E184"),sQuery(id+"F17.wireOp",EDGE,"E185")])]})});
            var Q9;
            {var subQ0=sQuery(id+"F0.wireOp",EDGE,"E30");var subQ1=sQuery(id+"F0.wireOp",EDGE,"E29");Q9=makeQuery(id+"F18.boolean.opBoolean","MERGE",EDGE,{"derivedFrom":[makeQuery(id+"F1.opExtrude","SWEPT_EDGE",EDGE,{"disambiguationData":[OSD([subQ1,subQ0])]}),makeQuery(id+"F18.opExtrude","SWEPT_EDGE",EDGE,{"disambiguationData":[OSD([subQ1,subQ0,sQuery(id+"F17.wireOp",EDGE,"E184"),sQuery(id+"F17.wireOp",EDGE,"E197")])]})]});}
            var Q10;
            {var subQ0=sQuery(id+"F0.wireOp",EDGE,"E57");var subQ1=sQuery(id+"F0.wireOp",EDGE,"E56");Q10=makeQuery(id+"F20.boolean.opBoolean","MERGE",EDGE,{"derivedFrom":[makeQuery(id+"F1.opExtrude","SWEPT_EDGE",EDGE,{"disambiguationData":[OSD([subQ1,subQ0])]}),makeQuery(id+"F20.opExtrude","SWEPT_EDGE",EDGE,{"disambiguationData":[OSD([subQ1,subQ0,sQuery(id+"F19.wireOp",EDGE,"E198"),sQuery(id+"F19.wireOp",EDGE,"E212")])]})]});}
            var Q11;
            Q11=makeQuery(id+"F20.boolean.opBoolean","COPY",EDGE,{"derivedFrom":makeQuery(id+"F20.opExtrude","SWEPT_EDGE",EDGE,{"disambiguationData":[OSD([sQuery(id+"F19.wireOp",EDGE,"E198"),sQuery(id+"F19.wireOp",EDGE,"E199")])]})});
            var Q12;
            Q12=makeQuery(id+"F20.boolean.opBoolean","COPY",EDGE,{"derivedFrom":makeQuery(id+"F20.opExtrude","SWEPT_EDGE",EDGE,{"disambiguationData":[OSD([sQuery(id+"F19.wireOp",EDGE,"E199"),sQuery(id+"F19.wireOp",EDGE,"E200")])]})});
            var Q13;
            Q13=makeQuery(id+"F20.boolean.opBoolean","COPY",EDGE,{"derivedFrom":makeQuery(id+"F20.opExtrude","SWEPT_EDGE",EDGE,{"disambiguationData":[OSD([sQuery(id+"F19.wireOp",EDGE,"E200"),sQuery(id+"F19.wireOp",EDGE,"E201")])]})});
            var Q14;
            Q14=makeQuery(id+"F20.boolean.opBoolean","COPY",EDGE,{"derivedFrom":makeQuery(id+"F20.opExtrude","SWEPT_EDGE",EDGE,{"disambiguationData":[OSD([sQuery(id+"F19.wireOp",EDGE,"E201"),sQuery(id+"F19.wireOp",EDGE,"E202")])]})});
            var Q15;
            Q15=makeQuery(id+"F20.boolean.opBoolean","COPY",EDGE,{"derivedFrom":makeQuery(id+"F20.opExtrude","SWEPT_EDGE",EDGE,{"disambiguationData":[OSD([sQuery(id+"F19.wireOp",EDGE,"E206"),sQuery(id+"F19.wireOp",EDGE,"E207")])]})});
            var Q16;
            Q16=makeQuery(id+"F20.boolean.opBoolean","COPY",EDGE,{"derivedFrom":makeQuery(id+"F20.opExtrude","SWEPT_EDGE",EDGE,{"disambiguationData":[OSD([sQuery(id+"F19.wireOp",EDGE,"E205"),sQuery(id+"F19.wireOp",EDGE,"E206")])]})});
            var Q17;
            Q17=makeQuery(id+"F20.boolean.opBoolean","COPY",EDGE,{"derivedFrom":makeQuery(id+"F20.opExtrude","SWEPT_EDGE",EDGE,{"disambiguationData":[OSD([sQuery(id+"F19.wireOp",EDGE,"E203"),sQuery(id+"F19.wireOp",EDGE,"E204")])]})});
            var Q18;
            Q18=makeQuery(id+"F20.boolean.opBoolean","COPY",EDGE,{"derivedFrom":makeQuery(id+"F20.opExtrude","SWEPT_EDGE",EDGE,{"disambiguationData":[OSD([sQuery(id+"F19.wireOp",EDGE,"E204"),sQuery(id+"F19.wireOp",EDGE,"E205")])]})});
            var Q19;
            Q19=makeQuery(id+"F20.boolean.opBoolean","COPY",EDGE,{"derivedFrom":makeQuery(id+"F20.opExtrude","SWEPT_EDGE",EDGE,{"disambiguationData":[OSD([sQuery(id+"F19.wireOp",EDGE,"E202"),sQuery(id+"F19.wireOp",EDGE,"E203")])]})});
            var Q20;
            Q20=makeQuery(id+"F20.boolean.opBoolean","COPY",EDGE,{"derivedFrom":makeQuery(id+"F20.opExtrude","SWEPT_EDGE",EDGE,{"disambiguationData":[OSD([sQuery(id+"F19.wireOp",EDGE,"E207"),sQuery(id+"F19.wireOp",EDGE,"E208")])]})});
            fillet(context, id + "F21", {"entities" : qUnion([Q0, Q1, Q2, Q3, Q4, Q5, Q6, Q7, Q8, Q9, Q10, Q11, Q12, Q13, Q14, Q15, Q16, Q17, Q18, Q19, Q20]), "radius" : 5.08 * mm, "tangentPropagation" : true, "allowEdgeOverflow" : false});
        }
        {
            var Q0;
            Q0=makeQuery(id+"F1.opExtrude","SWEPT_EDGE",EDGE,{"disambiguationData":[OSD([sQuery(id+"F0.wireOp",EDGE,"E0"),sQuery(id+"F0.wireOp",EDGE,"E1")])]});
            var Q1;
            Q1=makeQuery(id+"F1.opExtrude","SWEPT_EDGE",EDGE,{"disambiguationData":[OSD([sQuery(id+"F0.wireOp",EDGE,"E2"),sQuery(id+"F0.wireOp",EDGE,"E3")])]});
            var Q2;
            Q2=makeQuery(id+"F1.opExtrude","SWEPT_EDGE",EDGE,{"disambiguationData":[OSD([sQuery(id+"F0.wireOp",EDGE,"E1"),sQuery(id+"F0.wireOp",EDGE,"E2")])]});
            fillet(context, id + "F22", {"entities" : qUnion([Q0, Q1, Q2]), "radius" : 1.02 * mm, "tangentPropagation" : true, "allowEdgeOverflow" : false});
        }
        {
            var Q0;
            Q0=makeQuery(id+"F1.opExtrude","CAP_FACE",FACE,{"disambiguationData":[OSD([sQuery(id+"F0.wireOp",EDGE,"E0"),sQuery(id+"F0.wireOp",EDGE,"E1"),sQuery(id+"F0.wireOp",EDGE,"E2"),sQuery(id+"F0.wireOp",EDGE,"E3"),sQuery(id+"F0.wireOp",EDGE,"E4"),sQuery(id+"F0.wireOp",EDGE,"E5"),sQuery(id+"F0.wireOp",EDGE,"E6"),sQuery(id+"F0.wireOp",EDGE,"E7"),sQuery(id+"F0.wireOp",EDGE,"E8"),sQuery(id+"F0.wireOp",EDGE,"E9"),sQuery(id+"F0.wireOp",EDGE,"E10"),sQuery(id+"F0.wireOp",EDGE,"E11"),sQuery(id+"F0.wireOp",EDGE,"E12"),sQuery(id+"F0.wireOp",EDGE,"E13"),sQuery(id+"F0.wireOp",EDGE,"E14"),sQuery(id+"F0.wireOp",EDGE,"E15"),sQuery(id+"F0.wireOp",EDGE,"E16"),sQuery(id+"F0.wireOp",EDGE,"E17"),sQuery(id+"F0.wireOp",EDGE,"E18"),sQuery(id+"F0.wireOp",EDGE,"E19"),sQuery(id+"F0.wireOp",EDGE,"E20"),sQuery(id+"F0.wireOp",EDGE,"E21"),sQuery(id+"F0.wireOp",EDGE,"E22"),sQuery(id+"F0.wireOp",EDGE,"E23"),sQuery(id+"F0.wireOp",EDGE,"E24"),sQuery(id+"F0.wireOp",EDGE,"E25"),sQuery(id+"F0.wireOp",EDGE,"E26"),sQuery(id+"F0.wireOp",EDGE,"E27"),sQuery(id+"F0.wireOp",EDGE,"E28"),sQuery(id+"F0.wireOp",EDGE,"E29"),sQuery(id+"F0.wireOp",EDGE,"E30"),sQuery(id+"F0.wireOp",EDGE,"E31"),sQuery(id+"F0.wireOp",EDGE,"E32"),sQuery(id+"F0.wireOp",EDGE,"E33"),sQuery(id+"F0.wireOp",EDGE,"E34"),sQuery(id+"F0.wireOp",EDGE,"E35"),sQuery(id+"F0.wireOp",EDGE,"E36"),sQuery(id+"F0.wireOp",EDGE,"E37"),sQuery(id+"F0.wireOp",EDGE,"E38"),sQuery(id+"F0.wireOp",EDGE,"E39"),sQuery(id+"F0.wireOp",EDGE,"E40"),sQuery(id+"F0.wireOp",EDGE,"E41"),sQuery(id+"F0.wireOp",EDGE,"E42"),sQuery(id+"F0.wireOp",EDGE,"E43"),sQuery(id+"F0.wireOp",EDGE,"E44"),sQuery(id+"F0.wireOp",EDGE,"E45"),sQuery(id+"F0.wireOp",EDGE,"E46"),sQuery(id+"F0.wireOp",EDGE,"E47"),sQuery(id+"F0.wireOp",EDGE,"E48"),sQuery(id+"F0.wireOp",EDGE,"E49"),sQuery(id+"F0.wireOp",EDGE,"E50"),sQuery(id+"F0.wireOp",EDGE,"E51"),sQuery(id+"F0.wireOp",EDGE,"E52"),sQuery(id+"F0.wireOp",EDGE,"E53"),sQuery(id+"F0.wireOp",EDGE,"E54"),sQuery(id+"F0.wireOp",EDGE,"E55"),sQuery(id+"F0.wireOp",EDGE,"E56"),sQuery(id+"F0.wireOp",EDGE,"E57"),sQuery(id+"F0.wireOp",EDGE,"E58"),sQuery(id+"F0.wireOp",EDGE,"E59"),sQuery(id+"F0.wireOp",EDGE,"E60"),sQuery(id+"F0.wireOp",EDGE,"E61"),sQuery(id+"F0.wireOp",EDGE,"E62"),sQuery(id+"F0.wireOp",EDGE,"E63"),sQuery(id+"F0.wireOp",EDGE,"E64"),sQuery(id+"F0.wireOp",EDGE,"E65"),sQuery(id+"F0.wireOp",EDGE,"E66"),sQuery(id+"F0.wireOp",EDGE,"E67"),sQuery(id+"F0.wireOp",EDGE,"E68"),sQuery(id+"F0.wireOp",EDGE,"E69"),sQuery(id+"F0.wireOp",EDGE,"E70"),sQuery(id+"F0.wireOp",EDGE,"E71"),sQuery(id+"F0.wireOp",EDGE,"E72"),sQuery(id+"F0.wireOp",EDGE,"E73"),sQuery(id+"F0.wireOp",EDGE,"E74"),sQuery(id+"F0.wireOp",EDGE,"E75"),sQuery(id+"F0.wireOp",EDGE,"E76"),sQuery(id+"F0.wireOp",EDGE,"E77"),sQuery(id+"F0.wireOp",EDGE,"E78"),sQuery(id+"F0.wireOp",EDGE,"E79"),sQuery(id+"F0.wireOp",EDGE,"E80"),sQuery(id+"F0.wireOp",EDGE,"E81"),sQuery(id+"F0.wireOp",EDGE,"E82"),sQuery(id+"F0.wireOp",EDGE,"E83"),sQuery(id+"F0.wireOp",EDGE,"E84"),sQuery(id+"F0.wireOp",EDGE,"E85"),sQuery(id+"F0.wireOp",EDGE,"E87"),sQuery(id+"F0.wireOp",EDGE,"E88"),sQuery(id+"F0.wireOp",EDGE,"E89"),sQuery(id+"F0.wireOp",EDGE,"E90"),sQuery(id+"F0.wireOp",EDGE,"E91"),sQuery(id+"F0.wireOp",EDGE,"E92"),sQuery(id+"F0.wireOp",EDGE,"E93"),sQuery(id+"F0.wireOp",EDGE,"E94"),sQuery(id+"F0.wireOp",EDGE,"E95"),sQuery(id+"F0.wireOp",EDGE,"E96"),sQuery(id+"F0.wireOp",EDGE,"E97"),sQuery(id+"F0.wireOp",EDGE,"E98"),sQuery(id+"F0.wireOp",EDGE,"E99"),sQuery(id+"F0.wireOp",EDGE,"E100"),sQuery(id+"F0.wireOp",EDGE,"E101"),sQuery(id+"F0.wireOp",EDGE,"E102"),sQuery(id+"F0.wireOp",EDGE,"E103"),sQuery(id+"F0.wireOp",EDGE,"E104"),sQuery(id+"F0.wireOp",EDGE,"E105"),sQuery(id+"F0.wireOp",EDGE,"E106"),sQuery(id+"F0.wireOp",EDGE,"E107"),sQuery(id+"F0.wireOp",EDGE,"E108"),sQuery(id+"F0.wireOp",EDGE,"E109"),sQuery(id+"F0.wireOp",EDGE,"E110"),sQuery(id+"F0.wireOp",EDGE,"E111"),sQuery(id+"F0.wireOp",EDGE,"E112"),sQuery(id+"F0.wireOp",EDGE,"E113"),sQuery(id+"F0.wireOp",EDGE,"E114"),sQuery(id+"F0.wireOp",EDGE,"E115"),sQuery(id+"F0.wireOp",EDGE,"E116"),sQuery(id+"F0.wireOp",EDGE,"E117"),sQuery(id+"F0.wireOp",EDGE,"E118"),sQuery(id+"F0.wireOp",EDGE,"E119"),sQuery(id+"F0.wireOp",EDGE,"E120"),sQuery(id+"F0.wireOp",EDGE,"E121"),sQuery(id+"F0.wireOp",EDGE,"E122"),sQuery(id+"F0.wireOp",EDGE,"E123"),sQuery(id+"F0.wireOp",EDGE,"E124"),sQuery(id+"F0.wireOp",EDGE,"E125")])],"isStart":false});
            var sketch = newSketch(context, id + "F23", { "sketchPlane" : qUnion([Q0])});
            skLineSegment(sketch, "E213", {"start": v(-124.82, 5.25) * mm, "end": v(-123.9, 5.65) * mm});
            skPoint(sketch, "E213.endSnap0", {"position": v(-123.9, 7.65) * mm});
            skLineSegment(sketch, "E214", {"start": v(-123.9, 5.65) * mm, "end": v(-122.97, 5.69) * mm});
            skLineSegment(sketch, "E215", {"start": v(-122.97, 5.69) * mm, "end": v(-122.16, 5.32) * mm});
            skLineSegment(sketch, "E216", {"start": v(-122.16, 5.32) * mm, "end": v(-121.9, 4.5) * mm});
            skLineSegment(sketch, "E217", {"start": v(-121.9, 4.5) * mm, "end": v(-121.68, 3.47) * mm});
            skLineSegment(sketch, "E218", {"start": v(-121.68, 3.47) * mm, "end": v(-121.68, 2.62) * mm});
            skLineSegment(sketch, "E219", {"start": v(-121.68, 2.62) * mm, "end": v(-121.72, 1.66) * mm});
            skLineSegment(sketch, "E220", {"start": v(-121.72, 1.66) * mm, "end": v(-121.83, 0.52) * mm});
            skLineSegment(sketch, "E221", {"start": v(-121.83, 0.52) * mm, "end": v(-122.12, 0) * mm});
            skLineSegment(sketch, "E222", {"start": v(-122.12, 0) * mm, "end": v(-122.6, -0.74) * mm});
            skLineSegment(sketch, "E223", {"start": v(-122.6, -0.74) * mm, "end": v(-122.9, -1.16) * mm});
            skLineSegment(sketch, "E224", {"start": v(-122.9, -1.16) * mm, "end": v(-123.5, -0.7) * mm});
            skLineSegment(sketch, "E225", {"start": v(-123.5, -0.7) * mm, "end": v(-123.82, -0.38) * mm});
            skLineSegment(sketch, "E226", {"start": v(-123.82, -0.38) * mm, "end": v(-124.13, 0) * mm});
            skLineSegment(sketch, "E227", {"start": v(-124.13, 0) * mm, "end": v(-124.33, 0.28) * mm});
            skLineSegment(sketch, "E228", {"start": v(-124.33, 0.28) * mm, "end": v(-124.53, 0.61) * mm});
            skLineSegment(sketch, "E229", {"start": v(-124.53, 0.61) * mm, "end": v(-124.73, 1.01) * mm});
            skLineSegment(sketch, "E230", {"start": v(-124.73, 1.01) * mm, "end": v(-124.92, 1.5) * mm});
            skLineSegment(sketch, "E231", {"start": v(-124.92, 1.5) * mm, "end": v(-125.03, 1.92) * mm});
            skLineSegment(sketch, "E232", {"start": v(-125.03, 1.92) * mm, "end": v(-125.12, 2.41) * mm});
            skLineSegment(sketch, "E233", {"start": v(-125.12, 2.41) * mm, "end": v(-125.16, 2.9) * mm});
            skLineSegment(sketch, "E234", {"start": v(-125.16, 2.9) * mm, "end": v(-125.17, 3.42) * mm});
            skLineSegment(sketch, "E235", {"start": v(-125.17, 3.42) * mm, "end": v(-125.15, 3.79) * mm});
            skLineSegment(sketch, "E236", {"start": v(-125.15, 3.79) * mm, "end": v(-125.1, 4.21) * mm});
            skLineSegment(sketch, "E237", {"start": v(-125.1, 4.21) * mm, "end": v(-125.02, 4.61) * mm});
            skLineSegment(sketch, "E238", {"start": v(-125.02, 4.61) * mm, "end": v(-124.93, 4.94) * mm});
            skLineSegment(sketch, "E239", {"start": v(-124.93, 4.94) * mm, "end": v(-124.82, 5.25) * mm});
            skSolve(sketch);
        }
        {
            var Q0;
            Q0=qSketchRegion(id+"F23",true);
            extrude(context, id + "F24", {"entities" : qUnion([Q0]), "operationType" : NewBodyOperationType.ADD, "depth" : 1.27 * mm});
        }
        {
            var Q0;
            Q0=makeQuery(id+"F24.opExtrude","CAP_EDGE",EDGE,{"disambiguationData":[OSD([sQuery(id+"F23.wireOp",EDGE,"E223")])],"isStart":false});
            var Q1;
            Q1=makeQuery(id+"F24.opExtrude","CAP_EDGE",EDGE,{"disambiguationData":[OSD([sQuery(id+"F23.wireOp",EDGE,"E222")])],"isStart":false});
            var Q2;
            Q2=makeQuery(id+"F24.opExtrude","CAP_EDGE",EDGE,{"disambiguationData":[OSD([sQuery(id+"F23.wireOp",EDGE,"E219")])],"isStart":false});
            var Q3;
            Q3=makeQuery(id+"F24.opExtrude","CAP_EDGE",EDGE,{"disambiguationData":[OSD([sQuery(id+"F23.wireOp",EDGE,"E216")])],"isStart":false});
            var Q4;
            Q4=makeQuery(id+"F24.opExtrude","CAP_EDGE",EDGE,{"disambiguationData":[OSD([sQuery(id+"F23.wireOp",EDGE,"E214")])],"isStart":false});
            var Q5;
            Q5=makeQuery(id+"F24.opExtrude","CAP_EDGE",EDGE,{"disambiguationData":[OSD([sQuery(id+"F23.wireOp",EDGE,"E215")])],"isStart":false});
            var Q6;
            Q6=makeQuery(id+"F24.opExtrude","CAP_EDGE",EDGE,{"disambiguationData":[OSD([sQuery(id+"F23.wireOp",EDGE,"E213")])],"isStart":false});
            var Q7;
            Q7=makeQuery(id+"F24.opExtrude","CAP_EDGE",EDGE,{"disambiguationData":[OSD([sQuery(id+"F23.wireOp",EDGE,"E217")])],"isStart":false});
            var Q8;
            Q8=makeQuery(id+"F24.opExtrude","CAP_EDGE",EDGE,{"disambiguationData":[OSD([sQuery(id+"F23.wireOp",EDGE,"E218")])],"isStart":false});
            var Q9;
            Q9=makeQuery(id+"F24.opExtrude","CAP_EDGE",EDGE,{"disambiguationData":[OSD([sQuery(id+"F23.wireOp",EDGE,"E220")])],"isStart":false});
            var Q10;
            Q10=makeQuery(id+"F24.opExtrude","CAP_EDGE",EDGE,{"disambiguationData":[OSD([sQuery(id+"F23.wireOp",EDGE,"E221")])],"isStart":false});
            fillet(context, id + "F25", {"entities" : qUnion([Q0, Q1, Q2, Q3, Q4, Q5, Q6, Q7, Q8, Q9, Q10]), "radius" : 0.76 * mm, "tangentPropagation" : true, "allowEdgeOverflow" : false});
        }
        {
            var Q0;
            {var subQ4=sQuery(id+"F0.wireOp",EDGE,"E3");var subQ5=sQuery(id+"F0.wireOp",EDGE,"E2");var subQ7=sQuery(id+"F0.wireOp",EDGE,"E1");var subQ8=sQuery(id+"F0.wireOp",EDGE,"E0");var subQ12=sQuery(id+"F0.wireOp",EDGE,"E57");var subQ13=sQuery(id+"F0.wireOp",EDGE,"E56");var subQ14=sQuery(id+"F0.wireOp",EDGE,"E8");var subQ15=sQuery(id+"F0.wireOp",EDGE,"E7");var subQ21=sQuery(id+"F0.wireOp",EDGE,"E117");var subQ22=sQuery(id+"F0.wireOp",EDGE,"E116");var subQ29=sQuery(id+"F0.wireOp",EDGE,"E10");var subQ30=sQuery(id+"F0.wireOp",EDGE,"E9");var subQ31=sQuery(id+"F0.wireOp",EDGE,"E85");var subQ32=sQuery(id+"F0.wireOp",EDGE,"E84");var subQ33=sQuery(id+"F0.wireOp",EDGE,"E29");var subQ34=sQuery(id+"F0.wireOp",EDGE,"E28");var subQ37=sQuery(id+"F0.wireOp",EDGE,"E27");var subQ38=sQuery(id+"F0.wireOp",EDGE,"E26");var subQ39=sQuery(id+"F0.wireOp",EDGE,"E24");var subQ40=sQuery(id+"F0.wireOp",EDGE,"E23");var subQ43=sQuery(id+"F0.wireOp",EDGE,"E22");var subQ44=sQuery(id+"F0.wireOp",EDGE,"E21");var subQ47=sQuery(id+"F0.wireOp",EDGE,"E20");var subQ48=sQuery(id+"F0.wireOp",EDGE,"E13");var subQ49=sQuery(id+"F0.wireOp",EDGE,"E12");var subQ50=sQuery(id+"F0.wireOp",EDGE,"E25");var subQ51=sQuery(id+"F0.wireOp",EDGE,"E16");var subQ52=sQuery(id+"F0.wireOp",EDGE,"E11");var subQ53=sQuery(id+"F0.wireOp",EDGE,"E51");var subQ54=sQuery(id+"F0.wireOp",EDGE,"E50");var subQ55=sQuery(id+"F0.wireOp",EDGE,"E55");var subQ56=sQuery(id+"F0.wireOp",EDGE,"E54");var subQ57=sQuery(id+"F0.wireOp",EDGE,"E53");var subQ58=sQuery(id+"F0.wireOp",EDGE,"E49");var subQ61=sQuery(id+"F0.wireOp",EDGE,"E52");var subQ68=sQuery(id+"F0.wireOp",EDGE,"E30");var subQ69=sQuery(id+"F0.wireOp",EDGE,"E18");var subQ70=sQuery(id+"F0.wireOp",EDGE,"E17");var subQ73=sQuery(id+"F0.wireOp",EDGE,"E93");var subQ74=sQuery(id+"F0.wireOp",EDGE,"E92");var subQ75=sQuery(id+"F0.wireOp",EDGE,"E5");var subQ76=sQuery(id+"F0.wireOp",EDGE,"E4");var subQ77=sQuery(id+"F0.wireOp",EDGE,"E19");var subQ78=sQuery(id+"F0.wireOp",EDGE,"E91");var subQ79=sQuery(id+"F0.wireOp",EDGE,"E88");var subQ80=sQuery(id+"F0.wireOp",EDGE,"E87");var subQ81=sQuery(id+"F0.wireOp",EDGE,"E83");var subQ82=sQuery(id+"F0.wireOp",EDGE,"E90");var subQ83=sQuery(id+"F0.wireOp",EDGE,"E89");var subQ84=sQuery(id+"F0.wireOp",EDGE,"E81");var subQ85=sQuery(id+"F0.wireOp",EDGE,"E110");var subQ86=sQuery(id+"F0.wireOp",EDGE,"E115");var subQ89=sQuery(id+"F0.wireOp",EDGE,"E79");var subQ90=sQuery(id+"F0.wireOp",EDGE,"E15");var subQ91=sQuery(id+"F0.wireOp",EDGE,"E122");var subQ92=sQuery(id+"F0.wireOp",EDGE,"E121");var subQ93=sQuery(id+"F0.wireOp",EDGE,"E6");var subQ94=sQuery(id+"F0.wireOp",EDGE,"E104");var subQ95=sQuery(id+"F0.wireOp",EDGE,"E103");var subQ96=sQuery(id+"F0.wireOp",EDGE,"E102");var subQ97=sQuery(id+"F0.wireOp",EDGE,"E108");var subQ98=sQuery(id+"F0.wireOp",EDGE,"E80");var subQ99=sQuery(id+"F0.wireOp",EDGE,"E106");var subQ100=sQuery(id+"F0.wireOp",EDGE,"E105");var subQ101=sQuery(id+"F0.wireOp",EDGE,"E14");var subQ102=sQuery(id+"F0.wireOp",EDGE,"E109");var subQ103=sQuery(id+"F0.wireOp",EDGE,"E125");var subQ104=sQuery(id+"F0.wireOp",EDGE,"E124");var subQ105=sQuery(id+"F0.wireOp",EDGE,"E123");var subQ106=sQuery(id+"F0.wireOp",EDGE,"E120");var subQ107=sQuery(id+"F0.wireOp",EDGE,"E119");var subQ108=sQuery(id+"F0.wireOp",EDGE,"E118");var subQ109=sQuery(id+"F0.wireOp",EDGE,"E114");var subQ110=sQuery(id+"F0.wireOp",EDGE,"E113");var subQ111=sQuery(id+"F0.wireOp",EDGE,"E112");var subQ112=sQuery(id+"F0.wireOp",EDGE,"E111");var subQ113=sQuery(id+"F0.wireOp",EDGE,"E107");var subQ114=sQuery(id+"F0.wireOp",EDGE,"E101");var subQ115=sQuery(id+"F0.wireOp",EDGE,"E100");var subQ116=sQuery(id+"F0.wireOp",EDGE,"E99");var subQ117=sQuery(id+"F0.wireOp",EDGE,"E98");var subQ118=sQuery(id+"F0.wireOp",EDGE,"E97");var subQ119=sQuery(id+"F0.wireOp",EDGE,"E96");var subQ120=sQuery(id+"F0.wireOp",EDGE,"E95");var subQ121=sQuery(id+"F0.wireOp",EDGE,"E94");var subQ122=sQuery(id+"F0.wireOp",EDGE,"E82");var subQ123=sQuery(id+"F0.wireOp",EDGE,"E78");var subQ124=sQuery(id+"F0.wireOp",EDGE,"E77");var subQ125=sQuery(id+"F0.wireOp",EDGE,"E76");var subQ126=sQuery(id+"F0.wireOp",EDGE,"E75");var subQ127=sQuery(id+"F0.wireOp",EDGE,"E74");var subQ128=sQuery(id+"F0.wireOp",EDGE,"E73");var subQ129=sQuery(id+"F0.wireOp",EDGE,"E72");var subQ130=sQuery(id+"F0.wireOp",EDGE,"E71");var subQ131=sQuery(id+"F0.wireOp",EDGE,"E70");var subQ132=sQuery(id+"F0.wireOp",EDGE,"E69");var subQ133=sQuery(id+"F0.wireOp",EDGE,"E68");var subQ134=sQuery(id+"F0.wireOp",EDGE,"E67");var subQ135=sQuery(id+"F0.wireOp",EDGE,"E66");var subQ136=sQuery(id+"F0.wireOp",EDGE,"E65");var subQ137=sQuery(id+"F0.wireOp",EDGE,"E64");var subQ138=sQuery(id+"F0.wireOp",EDGE,"E63");var subQ139=sQuery(id+"F0.wireOp",EDGE,"E62");var subQ140=sQuery(id+"F0.wireOp",EDGE,"E61");var subQ141=sQuery(id+"F0.wireOp",EDGE,"E60");var subQ142=sQuery(id+"F0.wireOp",EDGE,"E59");var subQ143=sQuery(id+"F0.wireOp",EDGE,"E58");var subQ144=sQuery(id+"F0.wireOp",EDGE,"E48");var subQ145=sQuery(id+"F0.wireOp",EDGE,"E47");var subQ146=sQuery(id+"F0.wireOp",EDGE,"E46");var subQ147=sQuery(id+"F0.wireOp",EDGE,"E45");var subQ148=sQuery(id+"F0.wireOp",EDGE,"E44");var subQ149=sQuery(id+"F0.wireOp",EDGE,"E43");var subQ150=sQuery(id+"F0.wireOp",EDGE,"E42");var subQ151=sQuery(id+"F0.wireOp",EDGE,"E41");var subQ152=sQuery(id+"F0.wireOp",EDGE,"E40");var subQ153=sQuery(id+"F0.wireOp",EDGE,"E39");var subQ154=sQuery(id+"F0.wireOp",EDGE,"E38");var subQ155=sQuery(id+"F0.wireOp",EDGE,"E37");var subQ156=sQuery(id+"F0.wireOp",EDGE,"E36");var subQ157=sQuery(id+"F0.wireOp",EDGE,"E35");var subQ158=sQuery(id+"F0.wireOp",EDGE,"E34");var subQ159=sQuery(id+"F0.wireOp",EDGE,"E33");var subQ160=sQuery(id+"F0.wireOp",EDGE,"E32");var subQ161=sQuery(id+"F0.wireOp",EDGE,"E31");var subQ162=makeQuery(id+"F1.opExtrude","CAP_FACE",FACE,{"disambiguationData":[OSD([subQ8,subQ7,subQ5,subQ4,subQ76,subQ75,subQ93,subQ15,subQ14,subQ30,subQ29,subQ52,subQ49,subQ48,subQ101,subQ90,subQ51,subQ70,subQ69,subQ77,subQ47,subQ44,subQ43,subQ40,subQ39,subQ50,subQ38,subQ37,subQ34,subQ33,subQ68,subQ161,subQ160,subQ159,subQ158,subQ157,subQ156,subQ155,subQ154,subQ153,subQ152,subQ151,subQ150,subQ149,subQ148,subQ147,subQ146,subQ145,subQ144,subQ58,subQ54,subQ53,subQ61,subQ57,subQ56,subQ55,subQ13,subQ12,subQ143,subQ142,subQ141,subQ140,subQ139,subQ138,subQ137,subQ136,subQ135,subQ134,subQ133,subQ132,subQ131,subQ130,subQ129,subQ128,subQ127,subQ126,subQ125,subQ124,subQ123,subQ89,subQ98,subQ84,subQ122,subQ81,subQ32,subQ31,subQ80,subQ79,subQ83,subQ82,subQ78,subQ74,subQ73,subQ121,subQ120,subQ119,subQ118,subQ117,subQ116,subQ115,subQ114,subQ96,subQ95,subQ94,subQ100,subQ99,subQ113,subQ97,subQ102,subQ85,subQ112,subQ111,subQ110,subQ109,subQ86,subQ22,subQ21,subQ108,subQ107,subQ106,subQ92,subQ91,subQ105,subQ104,subQ103])],"isStart":false});Q0=makeQuery(id+"F24.boolean.opBoolean","SPLIT",FACE,{"disambiguationData":[TD([makeQuery(id+"F1.opExtrude","SWEPT_FACE",FACE,{"disambiguationData":[OSD([subQ8])]})])],"derivedFrom":subQ162});}
            var sketch = newSketch(context, id + "F26", { "sketchPlane" : qUnion([Q0])});
            skLineSegment(sketch, "E240", {"start": v(-127.9, 0) * mm, "end": v(-127.9, 65.62) * mm});
            skLineSegment(sketch, "E241", {"start": v(-128.69, -58.53) * mm, "end": v(-127.9, 0) * mm});
            skLineSegment(sketch, "E242", {"start": v(-20.66, 65.62) * mm, "end": v(-20.66, -88.9) * mm});
            skLineSegment(sketch, "E243.bottom", {"start": v(-20.66, 65.62) * mm, "end": v(-163.83, 65.62) * mm});
            skLineSegment(sketch, "E243.top", {"start": v(-20.66, -111.8) * mm, "end": v(-163.83, -111.8) * mm});
            skLineSegment(sketch, "E243.left", {"start": v(-20.66, 65.62) * mm, "end": v(-20.66, -111.8) * mm});
            skLineSegment(sketch, "E243.right", {"start": v(-163.83, 65.62) * mm, "end": v(-163.83, -111.8) * mm});
            skSolve(sketch);
        }
        {
            var Q0;
            Q0 = qSketchRegion(id + "F26", true);
            extrude(context, id + "F27", {"entities" : qUnion([Q0]), "operationType" : NewBodyOperationType.REMOVE, "oppositeDirection" : true, "depth" : 25.4 * mm});
        }
        {
            var Q0;
            Q0=makeQuery(id+"F24.opExtrude","CAP_FACE",FACE,{"disambiguationData":[OSD([sQuery(id+"F23.wireOp",EDGE,"E213"),sQuery(id+"F23.wireOp",EDGE,"E214"),sQuery(id+"F23.wireOp",EDGE,"E215"),sQuery(id+"F23.wireOp",EDGE,"E216"),sQuery(id+"F23.wireOp",EDGE,"E217"),sQuery(id+"F23.wireOp",EDGE,"E218"),sQuery(id+"F23.wireOp",EDGE,"E219"),sQuery(id+"F23.wireOp",EDGE,"E220"),sQuery(id+"F23.wireOp",EDGE,"E221"),sQuery(id+"F23.wireOp",EDGE,"E222"),sQuery(id+"F23.wireOp",EDGE,"E223"),sQuery(id+"F23.wireOp",EDGE,"E224"),sQuery(id+"F23.wireOp",EDGE,"E225"),sQuery(id+"F23.wireOp",EDGE,"E226"),sQuery(id+"F23.wireOp",EDGE,"E227"),sQuery(id+"F23.wireOp",EDGE,"E228"),sQuery(id+"F23.wireOp",EDGE,"E229"),sQuery(id+"F23.wireOp",EDGE,"E230"),sQuery(id+"F23.wireOp",EDGE,"E231"),sQuery(id+"F23.wireOp",EDGE,"E232"),sQuery(id+"F23.wireOp",EDGE,"E233"),sQuery(id+"F23.wireOp",EDGE,"E234"),sQuery(id+"F23.wireOp",EDGE,"E235"),sQuery(id+"F23.wireOp",EDGE,"E236"),sQuery(id+"F23.wireOp",EDGE,"E237"),sQuery(id+"F23.wireOp",EDGE,"E238"),sQuery(id+"F23.wireOp",EDGE,"E239")])],"isStart":false});
            var sketch = newSketch(context, id + "F28", { "sketchPlane" : qUnion([Q0])});
            skCircle(sketch, "E244", {"center": v(-124.73, 1.01) * mm, "radius": 27.64 * mm});
            skSolve(sketch);
        }
        {
            var Q0;
            Q0 = qSketchRegion(id + "F28", true);
            extrude(context, id + "F29", {"entities" : qUnion([Q0]), "operationType" : NewBodyOperationType.REMOVE, "oppositeDirection" : true, "depth" : 25.4 * mm});
        }
        {
            var Q0;
            Q0=makeQuery(id+"F27.boolean.opBoolean","COPY",FACE,{"derivedFrom":makeQuery(id+"F27.opExtrude","SWEPT_FACE",FACE,{"disambiguationData":[OSD([sQuery(id+"F26.wireOp",EDGE,"E243.left")])]})});
            var sketch = newSketch(context, id + "F30", { "sketchPlane" : qUnion([Q0])});
            skLineSegment(sketch, "E245.bottom", {"start": v(8.91, 5.08) * mm, "end": v(-59.5, 5.08) * mm});
            skLineSegment(sketch, "E245.top", {"start": v(8.91, 0) * mm, "end": v(-59.5, 0) * mm});
            skLineSegment(sketch, "E245.left", {"start": v(8.91, 5.08) * mm, "end": v(8.91, 0) * mm});
            skLineSegment(sketch, "E245.right", {"start": v(-59.5, 5.08) * mm, "end": v(-59.5, 0) * mm});
            skSolve(sketch);
        }
        {
            var Q0;
            Q0 = qSketchRegion(id + "F30", true);
            extrude(context, id + "F31", {"entities" : qUnion([Q0]), "operationType" : NewBodyOperationType.ADD, "depth" : 5.08 * mm});
        }
        {
            var Q0;
            Q0=makeQuery(id+"F31.opExtrude","SWEPT_FACE",FACE,{"disambiguationData":[OSD([sQuery(id+"F30.wireOp",EDGE,"E245.left")])]});
            var sketch = newSketch(context, id + "F32", { "sketchPlane" : qUnion([Q0])});
            skCircle(sketch, "E246", {"center": v(-25.74, 5.08) * mm, "radius": 5.08 * mm});
            skSolve(sketch);
        }
        {
            var Q0;
            Q0 = qSketchRegion(id + "F32", true);
            extrude(context, id + "F33", {"entities" : qUnion([Q0]), "operationType" : NewBodyOperationType.ADD, "oppositeDirection" : true, "depth" : 68.33 * mm});
        }
        {
            var Q0;
            Q0=makeQuery(id+"F33.boolean.opBoolean","MERGE",FACE,{"derivedFrom":[makeQuery(id+"F31.opExtrude","SWEPT_FACE",FACE,{"disambiguationData":[OSD([sQuery(id+"F30.wireOp",EDGE,"E245.left")])]}),makeQuery(id+"F33.opExtrude","CAP_FACE",FACE,{"disambiguationData":[OSD([sQuery(id+"F32.wireOp",EDGE,"E246")])],"isStart":true})]});
            var sketch = newSketch(context, id + "F34", { "sketchPlane" : qUnion([Q0])});
            skCircle(sketch, "E247", {"center": v(-25.74, 5.08) * mm, "radius": 3.81 * mm});
            skSolve(sketch);
        }
        {
            var Q0;
            Q0 = qSketchRegion(id + "F34", true);
            extrude(context, id + "F35", {"entities" : qUnion([Q0]), "operationType" : NewBodyOperationType.REMOVE, "endBound" : BoundingType.THROUGH_ALL, "oppositeDirection" : true, "depth" : 25.4 * mm});
        }
        {
            var Q0;
            Q0=makeQuery(id+"F31.boolean.opBoolean","MERGE",FACE,{"derivedFrom":[makeQuery(id+"F1.opExtrude","CAP_FACE",FACE,{"disambiguationData":[OSD([sQuery(id+"F0.wireOp",EDGE,"E0"),sQuery(id+"F0.wireOp",EDGE,"E1"),sQuery(id+"F0.wireOp",EDGE,"E2"),sQuery(id+"F0.wireOp",EDGE,"E3"),sQuery(id+"F0.wireOp",EDGE,"E4"),sQuery(id+"F0.wireOp",EDGE,"E5"),sQuery(id+"F0.wireOp",EDGE,"E6"),sQuery(id+"F0.wireOp",EDGE,"E7"),sQuery(id+"F0.wireOp",EDGE,"E8"),sQuery(id+"F0.wireOp",EDGE,"E9"),sQuery(id+"F0.wireOp",EDGE,"E10"),sQuery(id+"F0.wireOp",EDGE,"E11"),sQuery(id+"F0.wireOp",EDGE,"E12"),sQuery(id+"F0.wireOp",EDGE,"E13"),sQuery(id+"F0.wireOp",EDGE,"E14"),sQuery(id+"F0.wireOp",EDGE,"E15"),sQuery(id+"F0.wireOp",EDGE,"E16"),sQuery(id+"F0.wireOp",EDGE,"E17"),sQuery(id+"F0.wireOp",EDGE,"E18"),sQuery(id+"F0.wireOp",EDGE,"E19"),sQuery(id+"F0.wireOp",EDGE,"E20"),sQuery(id+"F0.wireOp",EDGE,"E21"),sQuery(id+"F0.wireOp",EDGE,"E22"),sQuery(id+"F0.wireOp",EDGE,"E23"),sQuery(id+"F0.wireOp",EDGE,"E24"),sQuery(id+"F0.wireOp",EDGE,"E25"),sQuery(id+"F0.wireOp",EDGE,"E26"),sQuery(id+"F0.wireOp",EDGE,"E27"),sQuery(id+"F0.wireOp",EDGE,"E28"),sQuery(id+"F0.wireOp",EDGE,"E29"),sQuery(id+"F0.wireOp",EDGE,"E30"),sQuery(id+"F0.wireOp",EDGE,"E31"),sQuery(id+"F0.wireOp",EDGE,"E32"),sQuery(id+"F0.wireOp",EDGE,"E33"),sQuery(id+"F0.wireOp",EDGE,"E34"),sQuery(id+"F0.wireOp",EDGE,"E35"),sQuery(id+"F0.wireOp",EDGE,"E36"),sQuery(id+"F0.wireOp",EDGE,"E37"),sQuery(id+"F0.wireOp",EDGE,"E38"),sQuery(id+"F0.wireOp",EDGE,"E39"),sQuery(id+"F0.wireOp",EDGE,"E40"),sQuery(id+"F0.wireOp",EDGE,"E41"),sQuery(id+"F0.wireOp",EDGE,"E42"),sQuery(id+"F0.wireOp",EDGE,"E43"),sQuery(id+"F0.wireOp",EDGE,"E44"),sQuery(id+"F0.wireOp",EDGE,"E45"),sQuery(id+"F0.wireOp",EDGE,"E46"),sQuery(id+"F0.wireOp",EDGE,"E47"),sQuery(id+"F0.wireOp",EDGE,"E48"),sQuery(id+"F0.wireOp",EDGE,"E49"),sQuery(id+"F0.wireOp",EDGE,"E50"),sQuery(id+"F0.wireOp",EDGE,"E51"),sQuery(id+"F0.wireOp",EDGE,"E52"),sQuery(id+"F0.wireOp",EDGE,"E53"),sQuery(id+"F0.wireOp",EDGE,"E54"),sQuery(id+"F0.wireOp",EDGE,"E55"),sQuery(id+"F0.wireOp",EDGE,"E56"),sQuery(id+"F0.wireOp",EDGE,"E57"),sQuery(id+"F0.wireOp",EDGE,"E58"),sQuery(id+"F0.wireOp",EDGE,"E59"),sQuery(id+"F0.wireOp",EDGE,"E60"),sQuery(id+"F0.wireOp",EDGE,"E61"),sQuery(id+"F0.wireOp",EDGE,"E62"),sQuery(id+"F0.wireOp",EDGE,"E63"),sQuery(id+"F0.wireOp",EDGE,"E64"),sQuery(id+"F0.wireOp",EDGE,"E65"),sQuery(id+"F0.wireOp",EDGE,"E66"),sQuery(id+"F0.wireOp",EDGE,"E67"),sQuery(id+"F0.wireOp",EDGE,"E68"),sQuery(id+"F0.wireOp",EDGE,"E69"),sQuery(id+"F0.wireOp",EDGE,"E70"),sQuery(id+"F0.wireOp",EDGE,"E71"),sQuery(id+"F0.wireOp",EDGE,"E72"),sQuery(id+"F0.wireOp",EDGE,"E73"),sQuery(id+"F0.wireOp",EDGE,"E74"),sQuery(id+"F0.wireOp",EDGE,"E75"),sQuery(id+"F0.wireOp",EDGE,"E76"),sQuery(id+"F0.wireOp",EDGE,"E77"),sQuery(id+"F0.wireOp",EDGE,"E78"),sQuery(id+"F0.wireOp",EDGE,"E79"),sQuery(id+"F0.wireOp",EDGE,"E80"),sQuery(id+"F0.wireOp",EDGE,"E81"),sQuery(id+"F0.wireOp",EDGE,"E82"),sQuery(id+"F0.wireOp",EDGE,"E83"),sQuery(id+"F0.wireOp",EDGE,"E84"),sQuery(id+"F0.wireOp",EDGE,"E85"),sQuery(id+"F0.wireOp",EDGE,"E87"),sQuery(id+"F0.wireOp",EDGE,"E88"),sQuery(id+"F0.wireOp",EDGE,"E89"),sQuery(id+"F0.wireOp",EDGE,"E90"),sQuery(id+"F0.wireOp",EDGE,"E91"),sQuery(id+"F0.wireOp",EDGE,"E92"),sQuery(id+"F0.wireOp",EDGE,"E93"),sQuery(id+"F0.wireOp",EDGE,"E94"),sQuery(id+"F0.wireOp",EDGE,"E95"),sQuery(id+"F0.wireOp",EDGE,"E96"),sQuery(id+"F0.wireOp",EDGE,"E97"),sQuery(id+"F0.wireOp",EDGE,"E98"),sQuery(id+"F0.wireOp",EDGE,"E99"),sQuery(id+"F0.wireOp",EDGE,"E100"),sQuery(id+"F0.wireOp",EDGE,"E101"),sQuery(id+"F0.wireOp",EDGE,"E102"),sQuery(id+"F0.wireOp",EDGE,"E103"),sQuery(id+"F0.wireOp",EDGE,"E104"),sQuery(id+"F0.wireOp",EDGE,"E105"),sQuery(id+"F0.wireOp",EDGE,"E106"),sQuery(id+"F0.wireOp",EDGE,"E107"),sQuery(id+"F0.wireOp",EDGE,"E108"),sQuery(id+"F0.wireOp",EDGE,"E109"),sQuery(id+"F0.wireOp",EDGE,"E110"),sQuery(id+"F0.wireOp",EDGE,"E111"),sQuery(id+"F0.wireOp",EDGE,"E112"),sQuery(id+"F0.wireOp",EDGE,"E113"),sQuery(id+"F0.wireOp",EDGE,"E114"),sQuery(id+"F0.wireOp",EDGE,"E115"),sQuery(id+"F0.wireOp",EDGE,"E116"),sQuery(id+"F0.wireOp",EDGE,"E117"),sQuery(id+"F0.wireOp",EDGE,"E118"),sQuery(id+"F0.wireOp",EDGE,"E119"),sQuery(id+"F0.wireOp",EDGE,"E120"),sQuery(id+"F0.wireOp",EDGE,"E121"),sQuery(id+"F0.wireOp",EDGE,"E122"),sQuery(id+"F0.wireOp",EDGE,"E123"),sQuery(id+"F0.wireOp",EDGE,"E124"),sQuery(id+"F0.wireOp",EDGE,"E125")])],"isStart":true}),makeQuery(id+"F31.opExtrude","SWEPT_FACE",FACE,{"disambiguationData":[OSD([sQuery(id+"F30.wireOp",EDGE,"E245.top")])]})]});
            var sketch = newSketch(context, id + "F36", { "sketchPlane" : qUnion([Q0])});
            skLineSegment(sketch, "E248.bottom", {"start": v(-20.66, 8.91) * mm, "end": v(-34.67, 8.91) * mm});
            skLineSegment(sketch, "E248.top", {"start": v(-20.66, -4.8) * mm, "end": v(-34.67, -4.8) * mm});
            skLineSegment(sketch, "E248.left", {"start": v(-20.66, 8.91) * mm, "end": v(-20.66, -4.8) * mm});
            skLineSegment(sketch, "E248.right", {"start": v(-34.67, 8.91) * mm, "end": v(-34.67, -4.8) * mm});
            skLineSegment(sketch, "E249.bottom", {"start": v(-20.66, -4.8) * mm, "end": v(-37.14, -4.8) * mm});
            skLineSegment(sketch, "E249.top", {"start": v(-20.66, -18.52) * mm, "end": v(-37.14, -18.52) * mm});
            skLineSegment(sketch, "E249.left", {"start": v(-20.66, -4.8) * mm, "end": v(-20.66, -18.52) * mm});
            skLineSegment(sketch, "E249.right", {"start": v(-37.14, -4.8) * mm, "end": v(-37.14, -18.52) * mm});
            skLineSegment(sketch, "E250.bottom", {"start": v(-20.66, -18.52) * mm, "end": v(-38.33, -18.52) * mm});
            skLineSegment(sketch, "E250.top", {"start": v(-20.66, -32.23) * mm, "end": v(-38.33, -32.23) * mm});
            skLineSegment(sketch, "E250.left", {"start": v(-20.66, -18.52) * mm, "end": v(-20.66, -32.23) * mm});
            skLineSegment(sketch, "E250.right", {"start": v(-38.33, -18.52) * mm, "end": v(-38.33, -32.23) * mm});
            skLineSegment(sketch, "E251.bottom", {"start": v(-20.66, -32.23) * mm, "end": v(-39.27, -32.23) * mm});
            skLineSegment(sketch, "E251.top", {"start": v(-20.66, -45.95) * mm, "end": v(-39.27, -45.95) * mm});
            skLineSegment(sketch, "E251.left", {"start": v(-20.66, -32.23) * mm, "end": v(-20.66, -45.95) * mm});
            skLineSegment(sketch, "E251.right", {"start": v(-39.27, -32.23) * mm, "end": v(-39.27, -45.95) * mm});
            skLineSegment(sketch, "E252.bottom", {"start": v(-20.66, -45.95) * mm, "end": v(-39.37, -45.95) * mm});
            skLineSegment(sketch, "E252.top", {"start": v(-20.66, -59.67) * mm, "end": v(-39.37, -59.67) * mm});
            skLineSegment(sketch, "E252.left", {"start": v(-20.66, -45.95) * mm, "end": v(-20.66, -59.67) * mm});
            skLineSegment(sketch, "E252.right", {"start": v(-39.37, -45.95) * mm, "end": v(-39.37, -59.67) * mm});
            skSolve(sketch);
        }
        {
            var Q0;
            {var subQ1=sQuery(id+"F36.wireOp",EDGE,"E249.right");Q0=makeQuery(id+"F36.imprint","IMPRINT",FACE,{"disambiguationData":[TD([[makeQuery(id+"F36.imprint","IMPRINT",EDGE,{"derivedFrom":subQ1}),1.0]])]});}
            var Q1;
            {var subQ0=sQuery(id+"F36.wireOp",EDGE,"E249.left");Q1=makeQuery(id+"F36.imprint","IMPRINT",FACE,{"disambiguationData":[TD([[makeQuery(id+"F36.imprint","IMPRINT",EDGE,{"derivedFrom":subQ0}),-1.0]])]});}
            var Q2;
            {var subQ0=sQuery(id+"F36.wireOp",EDGE,"E251.left");Q2=makeQuery(id+"F36.imprint","IMPRINT",FACE,{"disambiguationData":[TD([[makeQuery(id+"F36.imprint","IMPRINT",EDGE,{"derivedFrom":subQ0}),-1.0]])]});}
            var Q3;
            {var subQ1=sQuery(id+"F36.wireOp",EDGE,"E251.right");Q3=makeQuery(id+"F36.imprint","IMPRINT",FACE,{"disambiguationData":[TD([[makeQuery(id+"F36.imprint","IMPRINT",EDGE,{"derivedFrom":subQ1}),1.0]])]});}
            extrude(context, id + "F37", {"entities" : qUnion([Q0, Q1, Q2, Q3]), "operationType" : NewBodyOperationType.REMOVE, "oppositeDirection" : true, "depth" : 25.4 * mm, "hasSecondDirection" : true, "secondDirectionOppositeDirection" : false, "secondDirectionDepth" : 25.4 * mm});
        }
    });
